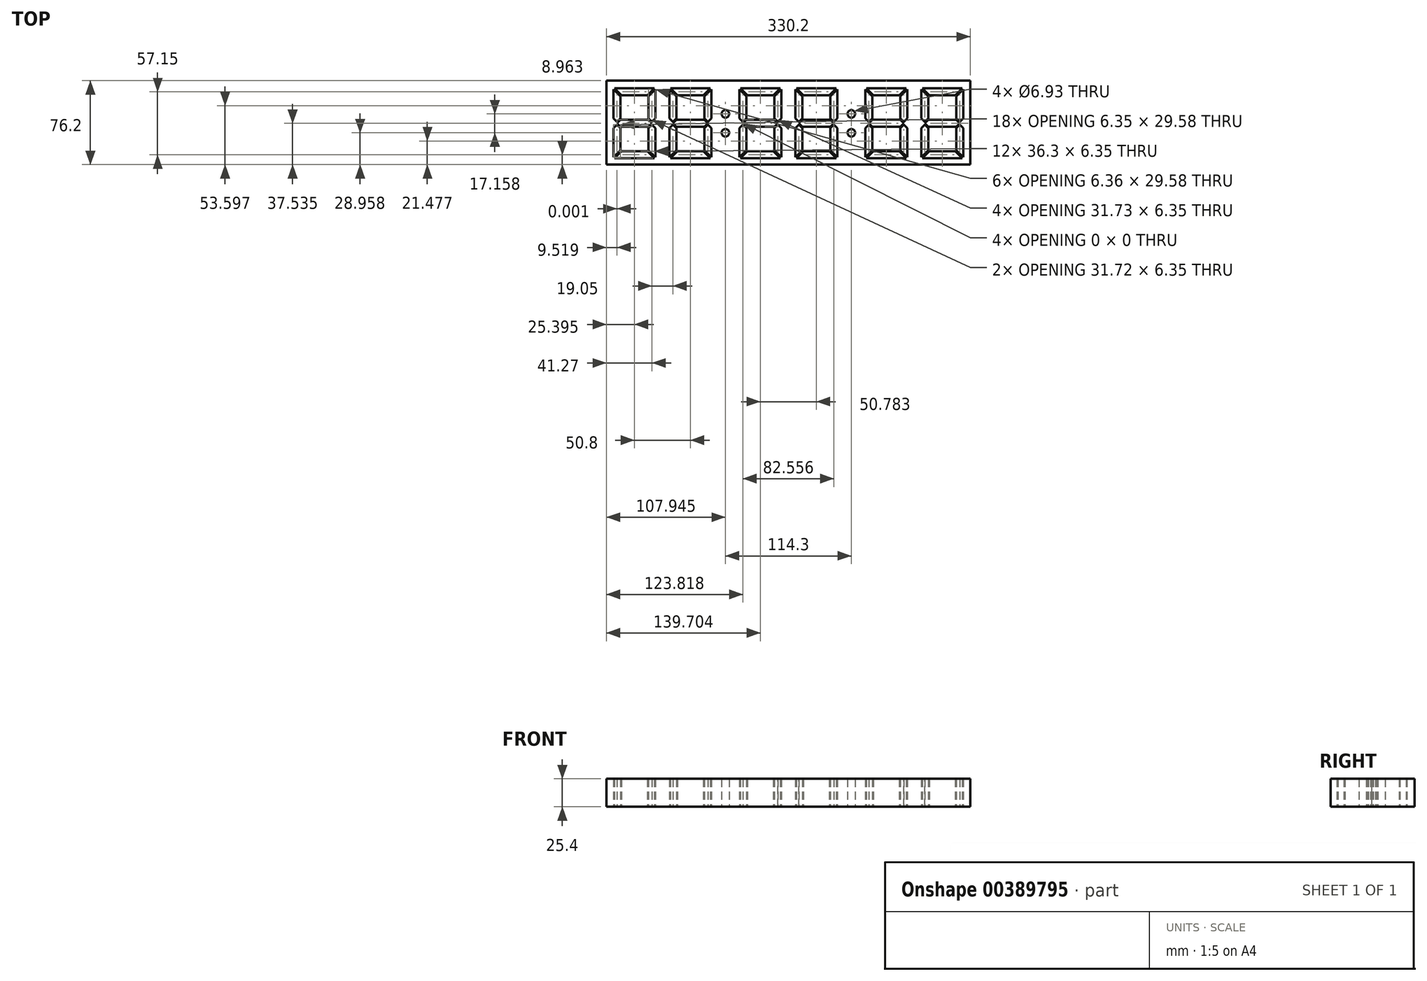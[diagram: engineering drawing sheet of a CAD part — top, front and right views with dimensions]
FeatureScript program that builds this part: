
annotation { "Feature Type Name" : "Feature", "Feature Type Description" : "" }
export const myFeature = defineFeature(function(context is Context, id is Id, definition is map)
    precondition{}
    {
        {
            var Q0;
            Q0=qCreatedBy(makeId("Top.planeOp"),FACE);
            var sketch = newSketch(context, id + "F0", { "sketchPlane" : qUnion([Q0])});
            skLineSegment(sketch, "E0.bottom", {"start": v(-71.32, 52.19) * mm, "end": v(-45.92, 52.19) * mm});
            skLineSegment(sketch, "E1.bottom", {"start": v(-64.08, 45.28) * mm, "end": v(-27.77, 45.28) * mm});
            skLineSegment(sketch, "E1.top", {"start": v(-64.08, -18.22) * mm, "end": v(-27.77, -18.22) * mm});
            skLineSegment(sketch, "E1.left", {"start": v(-64.98, 44.38) * mm, "end": v(-64.98, 18.04) * mm});
            skLineSegment(sketch, "E1.right", {"start": v(-26.87, 44.38) * mm, "end": v(-26.87, 18.04) * mm});
            skLineSegment(sketch, "E2.bottom", {"start": v(-57.73, 38.93) * mm, "end": v(-34.12, 38.93) * mm});
            skLineSegment(sketch, "E2.top", {"start": v(-57.73, -11.87) * mm, "end": v(-34.12, -11.87) * mm});
            skLineSegment(sketch, "E2.left", {"start": v(-58.62, 38.03) * mm, "end": v(-58.62, 17.97) * mm});
            skLineSegment(sketch, "E2.right", {"start": v(-33.22, 38.03) * mm, "end": v(-33.22, 17.97) * mm});
            skLineSegment(sketch, "E3", {"start": v(-45.92, 52.19) * mm, "end": v(-20.52, 52.19) * mm});
            skLineSegment(sketch, "E4", {"start": v(-61.35, 42.55) * mm, "end": v(-57.73, 38.93) * mm});
            skLineSegment(sketch, "E5", {"start": v(-62.25, 41.65) * mm, "end": v(-58.62, 38.03) * mm});
            skLineSegment(sketch, "E6", {"start": v(-62.25, 41.65) * mm, "end": v(-64.98, 44.38) * mm});
            skLineSegment(sketch, "E7", {"start": v(-61.35, 42.55) * mm, "end": v(-64.08, 45.28) * mm});
            skPoint(sketch, "E8.orphan", {"position": v(-64.98, 45.28) * mm});
            skPoint(sketch, "E9.orphan", {"position": v(-58.62, 38.93) * mm});
            skPoint(sketch, "E10.start.orphan", {"position": v(-61.8, 42.1) * mm});
            skLineSegment(sketch, "E11.MirrorCS", {"start": v(-29.6, 41.65) * mm, "end": v(-33.22, 38.03) * mm});
            skLineSegment(sketch, "E12.MirrorCS", {"start": v(-30.5, 42.55) * mm, "end": v(-34.12, 38.93) * mm});
            skPoint(sketch, "E13.MirrorP", {"position": v(-30.05, 42.1) * mm});
            skPoint(sketch, "E14.MirrorP", {"position": v(-26.87, 45.28) * mm});
            skLineSegment(sketch, "E15.MirrorCS", {"start": v(-30.5, 42.55) * mm, "end": v(-27.77, 45.28) * mm});
            skLineSegment(sketch, "E16.MirrorCS", {"start": v(-29.6, 41.65) * mm, "end": v(-26.87, 44.38) * mm});
            skPoint(sketch, "E17.MirrorP", {"position": v(-33.22, 38.93) * mm});
            skLineSegment(sketch, "E18.MirrorCS", {"start": v(-61.35, -15.5) * mm, "end": v(-57.73, -11.87) * mm});
            skPoint(sketch, "E19.MirrorP", {"position": v(-64.97, -18.22) * mm});
            skPoint(sketch, "E20.MirrorP", {"position": v(-61.8, -15.05) * mm});
            skLineSegment(sketch, "E21.MirrorCS", {"start": v(-29.6, -14.6) * mm, "end": v(-26.87, -17.32) * mm});
            skLineSegment(sketch, "E22.MirrorCS", {"start": v(-26.87, -17.32) * mm, "end": v(-26.87, 9) * mm});
            skLineSegment(sketch, "E23.MirrorCS", {"start": v(-29.6, -14.6) * mm, "end": v(-33.22, -10.97) * mm});
            skLineSegment(sketch, "E24.MirrorCS", {"start": v(-62.25, -14.6) * mm, "end": v(-64.98, -17.33) * mm});
            skPoint(sketch, "E25.MirrorP", {"position": v(-30.05, -15.05) * mm});
            skLineSegment(sketch, "E26.MirrorCS", {"start": v(-30.5, -15.5) * mm, "end": v(-27.77, -18.22) * mm});
            skPoint(sketch, "E27.MirrorP", {"position": v(-26.87, -18.22) * mm});
            skLineSegment(sketch, "E28.MirrorCS", {"start": v(-30.5, -15.5) * mm, "end": v(-34.12, -11.87) * mm});
            skPoint(sketch, "E29.MirrorP", {"position": v(-33.22, -11.87) * mm});
            skPoint(sketch, "E30.MirrorP", {"position": v(-58.62, -11.87) * mm});
            skLineSegment(sketch, "E31.MirrorCS", {"start": v(-64.98, -17.33) * mm, "end": v(-64.98, 9.01) * mm});
            skLineSegment(sketch, "E32.MirrorCS", {"start": v(-61.35, -15.5) * mm, "end": v(-64.08, -18.22) * mm});
            skPoint(sketch, "E33.MirrorCS.end.orphan", {"position": v(-42, 45.28) * mm});
            skPoint(sketch, "E33.MirrorCS.start.orphan", {"position": v(-42, 38.93) * mm});
            skPoint(sketch, "E34.end.orphan", {"position": v(-49.84, 45.28) * mm});
            skPoint(sketch, "E34.start.orphan", {"position": v(-49.84, 38.93) * mm});
            skPoint(sketch, "E35.end.orphan", {"position": v(-45.92, -24.57) * mm});
            skPoint(sketch, "E36.MirrorCS.end.orphan", {"position": v(-49.84, -18.22) * mm});
            skPoint(sketch, "E36.MirrorCS.start.orphan", {"position": v(-49.84, -11.87) * mm});
            skPoint(sketch, "E37.MirrorCS.end.orphan", {"position": v(-42, -18.22) * mm});
            skPoint(sketch, "E37.MirrorCS.start.orphan", {"position": v(-42, -11.87) * mm});
            skPoint(sketch, "E38.orphan", {"position": v(-58.62, 12.9) * mm});
            skPoint(sketch, "E39.orphan", {"position": v(-58.62, 14.16) * mm});
            skPoint(sketch, "E40.end.orphan", {"position": v(-64.97, 17.68) * mm});
            skPoint(sketch, "E41.MirrorCS.start.orphan", {"position": v(-58.3, 16.78) * mm});
            skPoint(sketch, "E42.MirrorCS.end.orphan", {"position": v(-64.97, 13.53) * mm});
            skPoint(sketch, "E43.MirrorP", {"position": v(-58.3, 10.28) * mm});
            skPoint(sketch, "E44.end.orphan", {"position": v(-64.98, 13.53) * mm});
            skLineSegment(sketch, "E45.trimOffspring", {"start": v(-64.98, 9.01) * mm, "end": v(-64.98, -17.33) * mm});
            skLineSegment(sketch, "E46.trimOffspring", {"start": v(-58.63, 9.08) * mm, "end": v(-58.63, -10.98) * mm});
            skPoint(sketch, "E47.trimOffspring.start.orphan", {"position": v(-64.97, 16.77) * mm});
            skPoint(sketch, "E48.trimOffspring.end.orphan", {"position": v(-26.87, 13.53) * mm});
            skLineSegment(sketch, "E49.MirrorCS", {"start": v(-26.87, 9) * mm, "end": v(-26.87, -17.32) * mm});
            skPoint(sketch, "E50.MirrorP", {"position": v(-33.54, 10.28) * mm});
            skPoint(sketch, "E51.MirrorP", {"position": v(-33.22, 12.9) * mm});
            skPoint(sketch, "E52.MirrorP", {"position": v(-33.54, 16.78) * mm});
            skLineSegment(sketch, "E53.MirrorCS", {"start": v(-26.87, -17.5) * mm, "end": v(-26.87, 9) * mm});
            skLineSegment(sketch, "E54.MirrorCS", {"start": v(-33.22, 9.08) * mm, "end": v(-33.22, -10.97) * mm});
            skPoint(sketch, "E55.MirrorP", {"position": v(-26.87, 16.77) * mm});
            skPoint(sketch, "E56.MirrorP", {"position": v(-26.87, 17.68) * mm});
            skPoint(sketch, "E57.MirrorP", {"position": v(-33.22, 14.16) * mm});
            skPoint(sketch, "E58.orphan", {"position": v(-64.98, -18.22) * mm});
            skLineSegment(sketch, "E59", {"start": v(-62.25, -14.6) * mm, "end": v(-58.63, -10.98) * mm});
            skLineSegment(sketch, "E60", {"start": v(-58.62, 16.7) * mm, "end": v(-61.78, 13.54) * mm});
            skPoint(sketch, "E61.trimOffspring.end.orphan", {"position": v(-58.62, 13.97) * mm});
            skPoint(sketch, "E62.right.start.orphan", {"position": v(-58.62, 13.53) * mm});
            skPoint(sketch, "E63.trimOffspring.end.orphan", {"position": v(-71.32, 13.8) * mm});
            skPoint(sketch, "E64.orphan", {"position": v(-61.8, 16.7) * mm});
            skLineSegment(sketch, "E65", {"start": v(-61.77, 14.8) * mm, "end": v(-58.62, 17.97) * mm});
            skLineSegment(sketch, "E66.MirrorCS", {"start": v(-61.77, 14.8) * mm, "end": v(-64.9, 17.97) * mm});
            skPoint(sketch, "E67.MirrorP", {"position": v(-61.8, 10.35) * mm});
            skLineSegment(sketch, "E68.MirrorCS", {"start": v(-61.77, 12.25) * mm, "end": v(-58.63, 9.08) * mm});
            skLineSegment(sketch, "E69.MirrorCS", {"start": v(-61.77, 12.25) * mm, "end": v(-64.9, 9.08) * mm});
            skLineSegment(sketch, "E70", {"start": v(-58.62, 16.7) * mm, "end": v(-33.22, 16.7) * mm});
            skLineSegment(sketch, "E71", {"start": v(-58.63, 10.35) * mm, "end": v(-33.23, 10.35) * mm});
            skLineSegment(sketch, "E72", {"start": v(-61.78, 13.54) * mm, "end": v(-58.63, 10.35) * mm});
            skLineSegment(sketch, "E73", {"start": v(-64.9, 17.97) * mm, "end": v(-64.98, 18.04) * mm});
            skPoint(sketch, "E74.orphan", {"position": v(-64.98, 17.1) * mm});
            skPoint(sketch, "E75.end.orphan", {"position": v(-64.97, 16.7) * mm});
            skPoint(sketch, "E76.trimOffspring.end.orphan", {"position": v(-58.63, 9.96) * mm});
            skLineSegment(sketch, "E77", {"start": v(-64.9, 9.08) * mm, "end": v(-64.98, 9.01) * mm});
            skPoint(sketch, "E78.orphan", {"position": v(-64.98, 9.96) * mm});
            skLineSegment(sketch, "E79.MirrorCS", {"start": v(-30.08, 14.8) * mm, "end": v(-33.22, 17.97) * mm});
            skLineSegment(sketch, "E80.MirrorCS", {"start": v(-30.08, 14.8) * mm, "end": v(-26.94, 17.97) * mm});
            skLineSegment(sketch, "E81.MirrorCS", {"start": v(-33.22, 16.7) * mm, "end": v(-30.07, 13.54) * mm});
            skLineSegment(sketch, "E82.MirrorCS", {"start": v(-30.07, 13.54) * mm, "end": v(-33.22, 10.35) * mm});
            skLineSegment(sketch, "E83.MirrorCS", {"start": v(-30.08, 12.26) * mm, "end": v(-33.22, 9.08) * mm});
            skLineSegment(sketch, "E84.MirrorCS", {"start": v(-30.08, 12.26) * mm, "end": v(-26.94, 9.08) * mm});
            skPoint(sketch, "E85.orphan", {"position": v(-33.22, 13.53) * mm});
            skPoint(sketch, "E86.orphan", {"position": v(-33.22, 9.96) * mm});
            skLineSegment(sketch, "E87", {"start": v(-26.94, 9.08) * mm, "end": v(-26.87, 9) * mm});
            skPoint(sketch, "E88.orphan", {"position": v(-33.22, 17.1) * mm});
            skLineSegment(sketch, "E89", {"start": v(-26.94, 17.97) * mm, "end": v(-26.87, 18.04) * mm});
            skPoint(sketch, "E90.end.orphan", {"position": v(-26.87, 16.7) * mm});
            skLineSegment(sketch, "E91.bottom", {"start": v(-20.52, 52.19) * mm, "end": v(-14.17, 52.19) * mm});
            skLineSegment(sketch, "E91.top", {"start": v(-20.52, -24.01) * mm, "end": v(-7.82, -24.01) * mm});
            skLineSegment(sketch, "E92", {"start": v(-14.17, 52.19) * mm, "end": v(-7.82, 52.19) * mm});
            skCircle(sketch, "E93", {"center": v(-14.17, 22.1) * mm, "radius": 3.46 * mm});
            skPoint(sketch, "E94.orphan", {"position": v(-14.17, 52.19) * mm});
            skPoint(sketch, "E95.trimOffspring.end.orphan", {"position": v(-14.17, -24.01) * mm});
            skCircle(sketch, "E96.MirrorC", {"center": v(-14.17, 4.95) * mm, "radius": 3.46 * mm});
            skPoint(sketch, "E97.end.orphan", {"position": v(-7.82, 14.09) * mm});
            skPoint(sketch, "E98.end.orphan", {"position": v(-20.52, -24.57) * mm});
            skPoint(sketch, "E98.start.orphan", {"position": v(-20.52, 13.53) * mm});
            skPoint(sketch, "E99.start.orphan", {"position": v(-20.52, 13.8) * mm});
            skPoint(sketch, "E100.MirrorP", {"position": v(-77.67, 13.53) * mm});
            skPoint(sketch, "E101.MirrorP", {"position": v(-115.77, 13.53) * mm});
            skLineSegment(sketch, "E102.MirrorCS", {"start": v(-77.74, 9.08) * mm, "end": v(-77.67, 9.01) * mm});
            skLineSegment(sketch, "E103.MirrorCS", {"start": v(-115.7, 9.08) * mm, "end": v(-115.78, 9) * mm});
            skLineSegment(sketch, "E104.MirrorCS", {"start": v(-115.7, 17.97) * mm, "end": v(-115.77, 18.04) * mm});
            skLineSegment(sketch, "E105.MirrorCS", {"start": v(-109.42, 16.7) * mm, "end": v(-112.58, 13.54) * mm});
            skLineSegment(sketch, "E106.MirrorCS", {"start": v(-80.87, 13.54) * mm, "end": v(-84.02, 10.35) * mm});
            skLineSegment(sketch, "E107.MirrorCS", {"start": v(-84.03, 16.7) * mm, "end": v(-80.87, 13.54) * mm});
            skLineSegment(sketch, "E108.MirrorCS", {"start": v(-112.58, 13.54) * mm, "end": v(-109.42, 10.35) * mm});
            skLineSegment(sketch, "E109.MirrorCS", {"start": v(-77.74, 17.97) * mm, "end": v(-77.67, 18.04) * mm});
            skLineSegment(sketch, "E110.MirrorCS", {"start": v(-115.78, 9) * mm, "end": v(-115.77, -17.32) * mm});
            skLineSegment(sketch, "E111.MirrorCS", {"start": v(-80.88, 14.8) * mm, "end": v(-84.03, 17.97) * mm});
            skLineSegment(sketch, "E112.MirrorCS", {"start": v(-113.05, -14.6) * mm, "end": v(-115.77, -17.32) * mm});
            skLineSegment(sketch, "E113.MirrorCS", {"start": v(-80.88, 14.8) * mm, "end": v(-77.74, 17.97) * mm});
            skLineSegment(sketch, "E114.MirrorCS", {"start": v(-80.4, -14.6) * mm, "end": v(-77.67, -17.33) * mm});
            skLineSegment(sketch, "E115.MirrorCS", {"start": v(-80.88, 12.25) * mm, "end": v(-84.02, 9.08) * mm});
            skLineSegment(sketch, "E116.MirrorCS", {"start": v(-112.15, -15.5) * mm, "end": v(-114.88, -18.22) * mm});
            skLineSegment(sketch, "E117.MirrorCS", {"start": v(-80.88, 12.25) * mm, "end": v(-77.74, 9.08) * mm});
            skLineSegment(sketch, "E118.MirrorCS", {"start": v(-113.05, 41.65) * mm, "end": v(-115.77, 44.38) * mm});
            skLineSegment(sketch, "E119.MirrorCS", {"start": v(-81.3, -15.5) * mm, "end": v(-78.57, -18.22) * mm});
            skLineSegment(sketch, "E120.MirrorCS", {"start": v(-81.3, 42.55) * mm, "end": v(-78.57, 45.28) * mm});
            skLineSegment(sketch, "E121.MirrorCS", {"start": v(-112.57, 14.8) * mm, "end": v(-115.7, 17.97) * mm});
            skLineSegment(sketch, "E122.MirrorCS", {"start": v(-112.57, 14.8) * mm, "end": v(-109.42, 17.97) * mm});
            skLineSegment(sketch, "E123.MirrorCS", {"start": v(-112.15, 42.55) * mm, "end": v(-114.88, 45.28) * mm});
            skPoint(sketch, "E124.MirrorP", {"position": v(-84.02, 13.53) * mm});
            skLineSegment(sketch, "E125.MirrorCS", {"start": v(-109.42, 9.08) * mm, "end": v(-109.42, -10.97) * mm});
            skPoint(sketch, "E126.MirrorP", {"position": v(-84.02, 12.9) * mm});
            skLineSegment(sketch, "E127.MirrorCS", {"start": v(-109.42, 38.03) * mm, "end": v(-109.42, 17.97) * mm});
            skLineSegment(sketch, "E128.MirrorCS", {"start": v(-112.57, 12.26) * mm, "end": v(-109.42, 9.08) * mm});
            skLineSegment(sketch, "E129.MirrorCS", {"start": v(-115.77, 44.38) * mm, "end": v(-115.77, 18.04) * mm});
            skLineSegment(sketch, "E130.MirrorCS", {"start": v(-112.57, 12.26) * mm, "end": v(-115.7, 9.08) * mm});
            skLineSegment(sketch, "E131.MirrorCS", {"start": v(-80.4, 41.65) * mm, "end": v(-77.67, 44.38) * mm});
            skLineSegment(sketch, "E132.MirrorCS", {"start": v(-112.15, 42.55) * mm, "end": v(-108.53, 38.93) * mm});
            skPoint(sketch, "E133.MirrorP", {"position": v(-109.1, 16.78) * mm});
            skPoint(sketch, "E134.MirrorP", {"position": v(-109.1, 10.28) * mm});
            skPoint(sketch, "E135.MirrorP", {"position": v(-109.42, 12.9) * mm});
            skLineSegment(sketch, "E136.MirrorCS", {"start": v(-113.05, -14.6) * mm, "end": v(-109.42, -10.97) * mm});
            skPoint(sketch, "E137.MirrorP", {"position": v(-115.77, -18.22) * mm});
            skLineSegment(sketch, "E138.MirrorCS", {"start": v(-81.3, -15.5) * mm, "end": v(-84.92, -11.87) * mm});
            skLineSegment(sketch, "E139.MirrorCS", {"start": v(-81.3, 42.55) * mm, "end": v(-84.92, 38.93) * mm});
            skLineSegment(sketch, "E140.MirrorCS", {"start": v(-80.4, -14.6) * mm, "end": v(-84.02, -10.98) * mm});
            skPoint(sketch, "E141.MirrorP", {"position": v(-115.77, 45.28) * mm});
            skLineSegment(sketch, "E142.MirrorCS", {"start": v(-84.92, -11.87) * mm, "end": v(-108.53, -11.87) * mm});
            skPoint(sketch, "E143.MirrorP", {"position": v(-109.42, 13.53) * mm});
            skLineSegment(sketch, "E144.MirrorCS", {"start": v(-77.67, -17.33) * mm, "end": v(-77.67, 9.01) * mm});
            skPoint(sketch, "E145.MirrorP", {"position": v(-77.67, 16.77) * mm});
            skLineSegment(sketch, "E146.MirrorCS", {"start": v(-113.05, 41.65) * mm, "end": v(-109.42, 38.03) * mm});
            skPoint(sketch, "E147.MirrorP", {"position": v(-109.42, 14.16) * mm});
            skPoint(sketch, "E148.MirrorP", {"position": v(-122.12, 13.53) * mm});
            skPoint(sketch, "E149.MirrorP", {"position": v(-77.67, -18.22) * mm});
            skLineSegment(sketch, "E150.MirrorCS", {"start": v(-78.57, -18.22) * mm, "end": v(-114.88, -18.22) * mm});
            skPoint(sketch, "E151.MirrorP", {"position": v(-84.34, 16.78) * mm});
            skLineSegment(sketch, "E152.MirrorCS", {"start": v(-112.15, -15.5) * mm, "end": v(-108.53, -11.87) * mm});
            skPoint(sketch, "E153.MirrorP", {"position": v(-84.34, 10.28) * mm});
            skPoint(sketch, "E154.MirrorP", {"position": v(-84.03, 14.16) * mm});
            skLineSegment(sketch, "E155.MirrorCS", {"start": v(-115.77, -17.5) * mm, "end": v(-115.78, 9) * mm});
            skPoint(sketch, "E156.MirrorP", {"position": v(-115.78, 16.7) * mm});
            skLineSegment(sketch, "E157.MirrorCS", {"start": v(-80.4, 41.65) * mm, "end": v(-84.03, 38.03) * mm});
            skPoint(sketch, "E158.MirrorP", {"position": v(-84.02, 13.97) * mm});
            skLineSegment(sketch, "E159.MirrorCS", {"start": v(-115.77, -17.32) * mm, "end": v(-115.78, 9) * mm});
            skPoint(sketch, "E160.MirrorP", {"position": v(-109.42, -11.87) * mm});
            skPoint(sketch, "E161.MirrorP", {"position": v(-77.67, 45.28) * mm});
            skPoint(sketch, "E162.MirrorP", {"position": v(-77.68, 16.7) * mm});
            skPoint(sketch, "E163.MirrorP", {"position": v(-77.67, 9.96) * mm});
            skPoint(sketch, "E164.MirrorP", {"position": v(-92.8, -11.87) * mm});
            skPoint(sketch, "E165.MirrorP", {"position": v(-80.85, 42.1) * mm});
            skLineSegment(sketch, "E166.MirrorCS", {"start": v(-84.02, 9.08) * mm, "end": v(-84.02, -10.98) * mm});
            skPoint(sketch, "E167.MirrorP", {"position": v(-92.8, -18.22) * mm});
            skLineSegment(sketch, "E168.MirrorCS", {"start": v(-77.67, 9.01) * mm, "end": v(-77.67, -17.33) * mm});
            skPoint(sketch, "E169.MirrorP", {"position": v(-84.02, -11.87) * mm});
            skPoint(sketch, "E170.MirrorP", {"position": v(-100.64, 45.28) * mm});
            skPoint(sketch, "E171.MirrorP", {"position": v(-84.03, 38.93) * mm});
            skPoint(sketch, "E172.MirrorP", {"position": v(-84.02, 9.96) * mm});
            skPoint(sketch, "E173.MirrorP", {"position": v(-109.42, 9.96) * mm});
            skPoint(sketch, "E174.MirrorP", {"position": v(-109.42, 17.1) * mm});
            skPoint(sketch, "E175.MirrorP", {"position": v(-115.78, 16.77) * mm});
            skLineSegment(sketch, "E176.MirrorCS", {"start": v(-84.92, 38.93) * mm, "end": v(-108.53, 38.93) * mm});
            skPoint(sketch, "E177.MirrorP", {"position": v(-100.64, -18.22) * mm});
            skPoint(sketch, "E178.MirrorP", {"position": v(-115.77, 17.68) * mm});
            skPoint(sketch, "E179.MirrorP", {"position": v(-100.64, 38.93) * mm});
            skPoint(sketch, "E180.MirrorP", {"position": v(-80.85, 10.35) * mm});
            skPoint(sketch, "E181.MirrorP", {"position": v(-100.64, -11.87) * mm});
            skPoint(sketch, "E182.MirrorP", {"position": v(-92.8, 38.93) * mm});
            skPoint(sketch, "E183.MirrorP", {"position": v(-109.42, 38.93) * mm});
            skLineSegment(sketch, "E184.MirrorCS", {"start": v(-77.67, 44.38) * mm, "end": v(-77.67, 18.04) * mm});
            skPoint(sketch, "E185.MirrorP", {"position": v(-77.67, 17.1) * mm});
            skPoint(sketch, "E186.MirrorP", {"position": v(-112.6, 42.1) * mm});
            skLineSegment(sketch, "E187.MirrorCS", {"start": v(-84.03, 16.7) * mm, "end": v(-109.43, 16.7) * mm});
            skLineSegment(sketch, "E188.MirrorCS", {"start": v(-84.02, 10.35) * mm, "end": v(-109.42, 10.35) * mm});
            skLineSegment(sketch, "E189.MirrorCS", {"start": v(-84.03, 38.03) * mm, "end": v(-84.03, 17.97) * mm});
            skPoint(sketch, "E190.MirrorP", {"position": v(-112.6, -15.05) * mm});
            skPoint(sketch, "E191.MirrorP", {"position": v(-80.85, 16.7) * mm});
            skPoint(sketch, "E192.MirrorP", {"position": v(-77.67, 17.68) * mm});
            skPoint(sketch, "E193.MirrorP", {"position": v(-92.8, 45.28) * mm});
            skPoint(sketch, "E194.MirrorP", {"position": v(-80.85, -15.05) * mm});
            skPoint(sketch, "E195.MirrorP", {"position": v(-122.13, 13.8) * mm});
            skLineSegment(sketch, "E196.MirrorCS", {"start": v(-78.57, 45.28) * mm, "end": v(-114.88, 45.28) * mm});
            skLineSegment(sketch, "E197.bottom", {"start": v(-71.32, 52.19) * mm, "end": v(-122.12, 52.19) * mm});
            skLineSegment(sketch, "E197.top", {"start": v(-71.32, -24.01) * mm, "end": v(-122.12, -24.01) * mm});
            skLineSegment(sketch, "E197.right", {"start": v(-122.12, 52.19) * mm, "end": v(-122.12, -24.01) * mm});
            skLineSegment(sketch, "E198", {"start": v(-20.52, -24.01) * mm, "end": v(-71.32, -24.01) * mm});
            skPoint(sketch, "E199.orphan", {"position": v(-71.32, -24.57) * mm});
            skPoint(sketch, "E200.MirrorCS.start.orphan", {"position": v(-20.52, 51.63) * mm});
            skPoint(sketch, "E201.1.0.0", {"position": v(-7.83, 13.8) * mm});
            skLineSegment(sketch, "E201.1.0.1", {"start": v(93.78, 52.19) * mm, "end": v(100.13, 52.19) * mm});
            skLineSegment(sketch, "E201.1.0.2", {"start": v(30.28, 9.08) * mm, "end": v(30.28, -10.98) * mm});
            skLineSegment(sketch, "E201.1.0.3", {"start": v(30.27, 16.7) * mm, "end": v(4.87, 16.7) * mm});
            skPoint(sketch, "E201.1.0.4", {"position": v(81.08, -11.87) * mm});
            skLineSegment(sketch, "E201.1.0.5", {"start": v(93.78, -24.01) * mm, "end": v(106.48, -24.01) * mm});
            skPoint(sketch, "E201.1.0.6", {"position": v(72.3, -11.87) * mm});
            skPoint(sketch, "E201.1.0.7", {"position": v(52.5, -15.05) * mm});
            skPoint(sketch, "E201.1.0.8", {"position": v(33.45, 10.35) * mm});
            skLineSegment(sketch, "E201.1.0.9", {"start": v(35.73, 45.28) * mm, "end": v(-0.58, 45.28) * mm});
            skLineSegment(sketch, "E201.1.0.10", {"start": v(-1.47, 44.38) * mm, "end": v(-1.47, 18.04) * mm});
            skPoint(sketch, "E201.1.0.11", {"position": v(21.5, -18.22) * mm});
            skPoint(sketch, "E201.1.0.12", {"position": v(36.63, 9.96) * mm});
            skPoint(sketch, "E201.1.0.13", {"position": v(49.32, 9.96) * mm});
            skPoint(sketch, "E201.1.0.14", {"position": v(84.25, -15.05) * mm});
            skLineSegment(sketch, "E201.1.0.15", {"start": v(55.67, 10.35) * mm, "end": v(81.07, 10.35) * mm});
            skPoint(sketch, "E201.1.0.16", {"position": v(81.08, 38.93) * mm});
            skPoint(sketch, "E201.1.0.17", {"position": v(87.43, 45.28) * mm});
            skCircle(sketch, "E201.1.0.18", {"center": v(100.13, 4.95) * mm, "radius": 3.46 * mm});
            skPoint(sketch, "E201.1.0.19", {"position": v(42.98, -24.57) * mm});
            skLineSegment(sketch, "E201.1.0.20", {"start": v(81.08, 9.08) * mm, "end": v(81.08, -10.97) * mm});
            skPoint(sketch, "E201.1.0.21", {"position": v(33.45, -15.05) * mm});
            skPoint(sketch, "E201.1.0.22", {"position": v(29.96, 16.78) * mm});
            skPoint(sketch, "E201.1.0.23", {"position": v(81.08, 17.1) * mm});
            skPoint(sketch, "E201.1.0.25", {"position": v(49.33, 17.68) * mm});
            skPoint(sketch, "E201.1.0.26", {"position": v(72.3, 38.93) * mm});
            skLineSegment(sketch, "E201.1.0.27", {"start": v(29.38, 38.93) * mm, "end": v(5.77, 38.93) * mm});
            skPoint(sketch, "E201.1.0.28", {"position": v(81.08, 9.96) * mm});
            skLineSegment(sketch, "E201.1.0.29", {"start": v(4.88, 9.08) * mm, "end": v(4.88, -10.97) * mm});
            skPoint(sketch, "E201.1.0.30", {"position": v(55.68, 13.97) * mm});
            skPoint(sketch, "E201.1.0.31", {"position": v(-1.47, 17.68) * mm});
            skPoint(sketch, "E201.1.0.32", {"position": v(13.66, 38.93) * mm});
            skLineSegment(sketch, "E201.1.0.34", {"start": v(56.57, 38.93) * mm, "end": v(80.18, 38.93) * mm});
            skLineSegment(sketch, "E201.1.0.35", {"start": v(49.32, 44.38) * mm, "end": v(49.32, 18.04) * mm});
            skLineSegment(sketch, "E201.1.0.36", {"start": v(42.98, 52.19) * mm, "end": v(68.38, 52.19) * mm});
            skLineSegment(sketch, "E201.1.0.37", {"start": v(42.98, -24.01) * mm, "end": v(-7.82, -24.01) * mm});
            skPoint(sketch, "E201.1.0.38", {"position": v(36.63, -18.22) * mm});
            skPoint(sketch, "E201.1.0.39", {"position": v(30.28, 12.9) * mm});
            skPoint(sketch, "E201.1.0.40", {"position": v(87.43, 16.77) * mm});
            skPoint(sketch, "E201.1.0.41", {"position": v(30.27, 14.16) * mm});
            skPoint(sketch, "E201.1.0.42", {"position": v(13.66, 45.28) * mm});
            skPoint(sketch, "E201.1.0.43", {"position": v(-1.47, 13.53) * mm});
            skPoint(sketch, "E201.1.0.44", {"position": v(64.46, -11.87) * mm});
            skPoint(sketch, "E201.1.0.45", {"position": v(52.5, 42.1) * mm});
            skLineSegment(sketch, "E201.1.0.46", {"start": v(55.67, 9.08) * mm, "end": v(55.67, -10.98) * mm});
            skPoint(sketch, "E201.1.0.47", {"position": v(33.45, 16.7) * mm});
            skPoint(sketch, "E201.1.0.48", {"position": v(-1.47, 45.28) * mm});
            skLineSegment(sketch, "E201.1.0.49", {"start": v(93.78, -24.01) * mm, "end": v(42.98, -24.01) * mm});
            skPoint(sketch, "E201.1.0.50", {"position": v(49.32, 45.28) * mm});
            skPoint(sketch, "E201.1.0.51", {"position": v(56, 10.28) * mm});
            skLineSegment(sketch, "E201.1.0.52", {"start": v(55.68, 38.03) * mm, "end": v(55.68, 17.97) * mm});
            skLineSegment(sketch, "E201.1.0.53", {"start": v(42.98, 52.19) * mm, "end": v(-7.82, 52.19) * mm});
            skPoint(sketch, "E201.1.0.54", {"position": v(93.78, 13.8) * mm});
            skPoint(sketch, "E201.1.0.55", {"position": v(87.43, 13.53) * mm});
            skPoint(sketch, "E201.1.0.56", {"position": v(64.46, 45.28) * mm});
            skPoint(sketch, "E201.1.0.57", {"position": v(5.2, 16.78) * mm});
            skPoint(sketch, "E201.1.0.58", {"position": v(80.76, 10.28) * mm});
            skPoint(sketch, "E201.1.0.59", {"position": v(55.67, 9.96) * mm});
            skPoint(sketch, "E201.1.0.60", {"position": v(72.3, 45.28) * mm});
            skPoint(sketch, "E201.1.0.61", {"position": v(49.32, -18.22) * mm});
            skPoint(sketch, "E201.1.0.62", {"position": v(42.98, 13.8) * mm});
            skPoint(sketch, "E201.1.0.63", {"position": v(55.68, 13.53) * mm});
            skPoint(sketch, "E201.1.0.64", {"position": v(55.68, -11.87) * mm});
            skPoint(sketch, "E201.1.0.65", {"position": v(106.48, 14.09) * mm});
            skPoint(sketch, "E201.1.0.66", {"position": v(93.78, 13.53) * mm});
            skLineSegment(sketch, "E201.1.0.67", {"start": v(100.13, 52.19) * mm, "end": v(106.48, 52.19) * mm});
            skPoint(sketch, "E201.1.0.68", {"position": v(4.88, 12.9) * mm});
            skPoint(sketch, "E201.1.0.69", {"position": v(49.32, 13.53) * mm});
            skPoint(sketch, "E201.1.0.70", {"position": v(100.13, 52.19) * mm});
            skPoint(sketch, "E201.1.0.71", {"position": v(30.28, -11.87) * mm});
            skPoint(sketch, "E201.1.0.72", {"position": v(1.7, -15.05) * mm});
            skLineSegment(sketch, "E201.1.0.73", {"start": v(87.43, 44.38) * mm, "end": v(87.43, 18.04) * mm});
            skPoint(sketch, "E201.1.0.74", {"position": v(68.38, -24.57) * mm});
            skPoint(sketch, "E201.1.0.75", {"position": v(55.68, 12.9) * mm});
            skPoint(sketch, "E201.1.0.76", {"position": v(49.32, 17.1) * mm});
            skPoint(sketch, "E201.1.0.77", {"position": v(4.88, -11.87) * mm});
            skLineSegment(sketch, "E201.1.0.78", {"start": v(49.32, 9.01) * mm, "end": v(49.32, -17.33) * mm});
            skPoint(sketch, "E201.1.0.79", {"position": v(64.46, 38.93) * mm});
            skLineSegment(sketch, "E201.1.0.80", {"start": v(56.57, -11.87) * mm, "end": v(80.18, -11.87) * mm});
            skLineSegment(sketch, "E201.1.0.81", {"start": v(4.88, 38.03) * mm, "end": v(4.88, 17.97) * mm});
            skPoint(sketch, "E201.1.0.82", {"position": v(1.7, 42.1) * mm});
            skPoint(sketch, "E201.1.0.83", {"position": v(52.5, 10.35) * mm});
            skPoint(sketch, "E201.1.0.84", {"position": v(49.33, 16.7) * mm});
            skPoint(sketch, "E201.1.0.85", {"position": v(36.63, 17.68) * mm});
            skPoint(sketch, "E201.1.0.86", {"position": v(64.46, -18.22) * mm});
            skPoint(sketch, "E201.1.0.87", {"position": v(81.08, 12.9) * mm});
            skPoint(sketch, "E201.1.0.88", {"position": v(55.68, 38.93) * mm});
            skPoint(sketch, "E201.1.0.89", {"position": v(5.2, 10.28) * mm});
            skPoint(sketch, "E201.1.0.90", {"position": v(36.63, 13.53) * mm});
            skPoint(sketch, "E201.1.0.91", {"position": v(93.78, -24.57) * mm});
            skLineSegment(sketch, "E201.1.0.92", {"start": v(50.22, 45.28) * mm, "end": v(86.53, 45.28) * mm});
            skLineSegment(sketch, "E201.1.0.93", {"start": v(50.22, -18.22) * mm, "end": v(86.53, -18.22) * mm});
            skPoint(sketch, "E201.1.0.94", {"position": v(30.28, 9.96) * mm});
            skPoint(sketch, "E201.1.0.95", {"position": v(29.96, 10.28) * mm});
            skLineSegment(sketch, "E201.1.0.96", {"start": v(30.27, 38.03) * mm, "end": v(30.27, 17.97) * mm});
            skLineSegment(sketch, "E201.1.0.97", {"start": v(30.28, 10.35) * mm, "end": v(4.88, 10.35) * mm});
            skPoint(sketch, "E201.1.0.98", {"position": v(87.43, -18.22) * mm});
            skPoint(sketch, "E201.1.0.99", {"position": v(52.5, 16.7) * mm});
            skPoint(sketch, "E201.1.0.100", {"position": v(30.27, 38.93) * mm});
            skLineSegment(sketch, "E201.1.0.101", {"start": v(-1.47, -17.32) * mm, "end": v(-1.48, 9) * mm});
            skPoint(sketch, "E201.1.0.102", {"position": v(36.63, 45.28) * mm});
            skPoint(sketch, "E201.1.0.103", {"position": v(4.88, 17.1) * mm});
            skPoint(sketch, "E201.1.0.104", {"position": v(4.88, 9.96) * mm});
            skLineSegment(sketch, "E201.1.0.105", {"start": v(68.38, 52.19) * mm, "end": v(93.78, 52.19) * mm});
            skLineSegment(sketch, "E201.1.0.106", {"start": v(29.38, -11.87) * mm, "end": v(5.77, -11.87) * mm});
            skPoint(sketch, "E201.1.0.107", {"position": v(13.66, -11.87) * mm});
            skPoint(sketch, "E201.1.0.108", {"position": v(93.78, 51.63) * mm});
            skPoint(sketch, "E201.1.0.109", {"position": v(-7.82, 13.53) * mm});
            skLineSegment(sketch, "E201.1.0.110", {"start": v(35.73, -18.22) * mm, "end": v(-0.58, -18.22) * mm});
            skPoint(sketch, "E201.1.0.111", {"position": v(4.88, 38.93) * mm});
            skPoint(sketch, "E201.1.0.112", {"position": v(21.5, -11.87) * mm});
            skLineSegment(sketch, "E201.1.0.113", {"start": v(36.63, 44.38) * mm, "end": v(36.63, 18.04) * mm});
            skCircle(sketch, "E201.1.0.114", {"center": v(100.13, 22.1) * mm, "radius": 3.46 * mm});
            skPoint(sketch, "E201.1.0.115", {"position": v(21.5, 45.28) * mm});
            skLineSegment(sketch, "E201.1.0.116", {"start": v(36.63, -17.33) * mm, "end": v(36.63, 9.01) * mm});
            skPoint(sketch, "E201.1.0.117", {"position": v(21.5, 38.93) * mm});
            skLineSegment(sketch, "E201.1.0.118", {"start": v(55.68, 16.7) * mm, "end": v(81.08, 16.7) * mm});
            skPoint(sketch, "E201.1.0.119", {"position": v(13.66, -18.22) * mm});
            skPoint(sketch, "E201.1.0.120", {"position": v(33.45, 42.1) * mm});
            skPoint(sketch, "E201.1.0.121", {"position": v(84.25, 42.1) * mm});
            skPoint(sketch, "E201.1.0.122", {"position": v(72.3, -18.22) * mm});
            skPoint(sketch, "E201.1.0.123", {"position": v(56, 16.78) * mm});
            skPoint(sketch, "E201.1.0.124", {"position": v(100.13, -24.01) * mm});
            skPoint(sketch, "E201.1.0.125", {"position": v(80.76, 16.78) * mm});
            skPoint(sketch, "E201.1.0.126", {"position": v(-1.47, -18.22) * mm});
            skLineSegment(sketch, "E201.1.0.127", {"start": v(81.08, 38.03) * mm, "end": v(81.08, 17.97) * mm});
            skPoint(sketch, "E201.1.0.128", {"position": v(-1.48, 16.77) * mm});
            skLineSegment(sketch, "E201.1.0.129", {"start": v(87.43, -17.5) * mm, "end": v(87.43, 9) * mm});
            skPoint(sketch, "E201.1.0.130", {"position": v(36.62, 16.7) * mm});
            skLineSegment(sketch, "E201.1.0.131", {"start": v(56.57, -11.87) * mm, "end": v(80.18, -11.87) * mm});
            skLineSegment(sketch, "E201.1.0.132", {"start": v(4.88, 9.08) * mm, "end": v(4.88, -10.97) * mm});
            skPoint(sketch, "E201.1.0.133", {"position": v(55.68, 14.16) * mm});
            skPoint(sketch, "E201.1.0.134", {"position": v(49.33, -18.22) * mm});
            skPoint(sketch, "E201.1.0.135", {"position": v(4.88, 12.9) * mm});
            skPoint(sketch, "E201.1.0.136", {"position": v(36.63, 17.1) * mm});
            skLineSegment(sketch, "E201.1.0.137", {"start": v(81.08, 9.08) * mm, "end": v(81.08, -10.97) * mm});
            skLineSegment(sketch, "E201.1.0.138", {"start": v(36.63, 9.01) * mm, "end": v(36.63, -17.33) * mm});
            skLineSegment(sketch, "E201.1.0.139", {"start": v(33, 42.55) * mm, "end": v(29.38, 38.93) * mm});
            skPoint(sketch, "E201.1.0.140", {"position": v(-1.47, 45.28) * mm});
            skLineSegment(sketch, "E201.1.0.141", {"start": v(52.05, -14.6) * mm, "end": v(55.67, -10.98) * mm});
            skLineSegment(sketch, "E201.1.0.142", {"start": v(1.25, 41.65) * mm, "end": v(4.88, 38.03) * mm});
            skLineSegment(sketch, "E201.1.0.143", {"start": v(84.7, -14.6) * mm, "end": v(81.08, -10.97) * mm});
            skLineSegment(sketch, "E201.1.0.144", {"start": v(52.95, -15.5) * mm, "end": v(56.57, -11.87) * mm});
            skPoint(sketch, "E201.1.0.145", {"position": v(5.2, 10.28) * mm});
            skPoint(sketch, "E201.1.0.146", {"position": v(81.08, 14.16) * mm});
            skPoint(sketch, "E201.1.0.147", {"position": v(56, 10.28) * mm});
            skPoint(sketch, "E201.1.0.148", {"position": v(49.33, 16.77) * mm});
            skPoint(sketch, "E201.1.0.149", {"position": v(87.43, 45.28) * mm});
            skPoint(sketch, "E201.1.0.150", {"position": v(87.43, 13.53) * mm});
            skPoint(sketch, "E201.1.0.151", {"position": v(55.68, 12.9) * mm});
            skPoint(sketch, "E201.1.0.152", {"position": v(93.78, -24.57) * mm});
            skPoint(sketch, "E201.1.0.153", {"position": v(4.88, 14.16) * mm});
            skLineSegment(sketch, "E201.1.0.154", {"start": v(33.9, -14.6) * mm, "end": v(30.28, -10.98) * mm});
            skLineSegment(sketch, "E201.1.0.155", {"start": v(29.38, -11.87) * mm, "end": v(5.77, -11.87) * mm});
            skPoint(sketch, "E201.1.0.156", {"position": v(87.43, -18.22) * mm});
            skPoint(sketch, "E201.1.0.157", {"position": v(5.2, 16.78) * mm});
            skPoint(sketch, "E201.1.0.158", {"position": v(87.43, 16.7) * mm});
            skLineSegment(sketch, "E201.1.0.159", {"start": v(33, -15.5) * mm, "end": v(29.38, -11.87) * mm});
            skLineSegment(sketch, "E201.1.0.160", {"start": v(83.8, -15.5) * mm, "end": v(80.18, -11.87) * mm});
            skLineSegment(sketch, "E201.1.0.161", {"start": v(-1.48, 9) * mm, "end": v(-1.47, -17.32) * mm});
            skLineSegment(sketch, "E201.1.0.162", {"start": v(52.95, 42.55) * mm, "end": v(56.57, 38.93) * mm});
            skLineSegment(sketch, "E201.1.0.163", {"start": v(87.43, 44.38) * mm, "end": v(87.43, 18.04) * mm});
            skLineSegment(sketch, "E201.1.0.164", {"start": v(33.9, 41.65) * mm, "end": v(30.27, 38.03) * mm});
            skPoint(sketch, "E201.1.0.165", {"position": v(49.33, 13.53) * mm});
            skLineSegment(sketch, "E201.1.0.166", {"start": v(83.8, 42.55) * mm, "end": v(80.18, 38.93) * mm});
            skLineSegment(sketch, "E201.1.0.167", {"start": v(52.05, 41.65) * mm, "end": v(55.68, 38.03) * mm});
            skLineSegment(sketch, "E201.1.0.168", {"start": v(4.88, 38.03) * mm, "end": v(4.88, 17.97) * mm});
            skPoint(sketch, "E201.1.0.169", {"position": v(80.76, 16.78) * mm});
            skLineSegment(sketch, "E201.1.0.170", {"start": v(87.43, 9) * mm, "end": v(87.43, -17.32) * mm});
            skLineSegment(sketch, "E201.1.0.171", {"start": v(50.22, -18.22) * mm, "end": v(86.53, -18.22) * mm});
            skPoint(sketch, "E201.1.0.172", {"position": v(-1.47, 13.53) * mm});
            skLineSegment(sketch, "E201.1.0.173", {"start": v(-1.47, 44.38) * mm, "end": v(-1.47, 18.04) * mm});
            skPoint(sketch, "E201.1.0.174", {"position": v(81.08, 12.9) * mm});
            skLineSegment(sketch, "E201.1.0.175", {"start": v(84.7, 41.65) * mm, "end": v(81.08, 38.03) * mm});
            skPoint(sketch, "E201.1.0.176", {"position": v(30.28, 13.97) * mm});
            skPoint(sketch, "E201.1.0.177", {"position": v(80.76, 10.28) * mm});
            skPoint(sketch, "E201.1.0.178", {"position": v(30.28, 12.9) * mm});
            skLineSegment(sketch, "E201.1.0.179", {"start": v(2.15, -15.5) * mm, "end": v(5.77, -11.87) * mm});
            skPoint(sketch, "E201.1.0.180", {"position": v(29.96, 10.28) * mm});
            skPoint(sketch, "E201.1.0.181", {"position": v(-1.48, 16.7) * mm});
            skLineSegment(sketch, "E201.1.0.182", {"start": v(2.15, 42.55) * mm, "end": v(5.77, 38.93) * mm});
            skPoint(sketch, "E201.1.0.183", {"position": v(36.63, 13.53) * mm});
            skLineSegment(sketch, "E201.1.0.184", {"start": v(81.08, 38.03) * mm, "end": v(81.08, 17.97) * mm});
            skPoint(sketch, "E201.1.0.185", {"position": v(56, 16.78) * mm});
            skLineSegment(sketch, "E201.1.0.186", {"start": v(49.32, -17.33) * mm, "end": v(49.32, 9.01) * mm});
            skLineSegment(sketch, "E201.1.0.187", {"start": v(1.25, -14.6) * mm, "end": v(4.88, -10.97) * mm});
            skLineSegment(sketch, "E201.1.0.188", {"start": v(35.73, -18.22) * mm, "end": v(-0.58, -18.22) * mm});
            skPoint(sketch, "E201.1.0.189", {"position": v(29.96, 16.78) * mm});
            skPoint(sketch, "E201.1.0.190", {"position": v(87.43, 17.68) * mm});
            skPoint(sketch, "E201.1.0.191", {"position": v(-1.47, -18.22) * mm});
            skPoint(sketch, "E201.1.0.192", {"position": v(36.63, -18.22) * mm});
            skLineSegment(sketch, "E201.1.0.193", {"start": v(87.43, 44.38) * mm, "end": v(87.43, 18.04) * mm});
            skLineSegment(sketch, "E201.1.0.194", {"start": v(33, 42.55) * mm, "end": v(35.73, 45.28) * mm});
            skPoint(sketch, "E201.1.0.195", {"position": v(4.88, 13.53) * mm});
            skPoint(sketch, "E201.1.0.196", {"position": v(30.28, 13.53) * mm});
            skLineSegment(sketch, "E201.1.0.197", {"start": v(1.73, 14.8) * mm, "end": v(-1.4, 17.97) * mm});
            skLineSegment(sketch, "E201.1.0.198", {"start": v(1.73, 12.26) * mm, "end": v(4.88, 9.08) * mm});
            skPoint(sketch, "E201.1.0.199", {"position": v(36.63, 16.77) * mm});
            skLineSegment(sketch, "E201.1.0.200", {"start": v(81.08, 38.03) * mm, "end": v(81.08, 17.97) * mm});
            skLineSegment(sketch, "E201.1.0.201", {"start": v(4.88, 9.08) * mm, "end": v(4.88, -10.97) * mm});
            skLineSegment(sketch, "E201.1.0.202", {"start": v(33.9, 41.65) * mm, "end": v(36.63, 44.38) * mm});
            skLineSegment(sketch, "E201.1.0.203", {"start": v(1.73, 12.26) * mm, "end": v(-1.4, 9.08) * mm});
            skPoint(sketch, "E201.1.0.204", {"position": v(-1.47, 13.53) * mm});
            skPoint(sketch, "E201.1.0.205", {"position": v(49.33, 13.53) * mm});
            skLineSegment(sketch, "E201.1.0.206", {"start": v(4.88, 38.03) * mm, "end": v(4.88, 17.97) * mm});
            skLineSegment(sketch, "E201.1.0.207", {"start": v(-1.47, 44.38) * mm, "end": v(-1.47, 18.04) * mm});
            skLineSegment(sketch, "E201.1.0.208", {"start": v(52.05, 41.65) * mm, "end": v(49.32, 44.38) * mm});
            skLineSegment(sketch, "E201.1.0.209", {"start": v(52.95, 42.55) * mm, "end": v(50.22, 45.28) * mm});
            skPoint(sketch, "E201.1.0.210", {"position": v(36.63, 13.53) * mm});
            skLineSegment(sketch, "E201.1.0.211", {"start": v(84.22, 12.26) * mm, "end": v(81.08, 9.08) * mm});
            skLineSegment(sketch, "E201.1.0.212", {"start": v(52.53, 12.25) * mm, "end": v(55.67, 9.08) * mm});
            skLineSegment(sketch, "E201.1.0.213", {"start": v(1.73, 14.8) * mm, "end": v(4.88, 17.97) * mm});
            skLineSegment(sketch, "E201.1.0.214", {"start": v(-1.47, -17.5) * mm, "end": v(-1.48, 9) * mm});
            skLineSegment(sketch, "E201.1.0.215", {"start": v(81.08, 9.08) * mm, "end": v(81.08, -10.97) * mm});
            skLineSegment(sketch, "E201.1.0.216", {"start": v(87.43, 9) * mm, "end": v(87.43, -17.32) * mm});
            skPoint(sketch, "E201.1.0.217", {"position": v(81.08, 13.53) * mm});
            skPoint(sketch, "E201.1.0.218", {"position": v(87.43, 13.53) * mm});
            skLineSegment(sketch, "E201.1.0.219", {"start": v(84.22, 12.26) * mm, "end": v(87.36, 9.08) * mm});
            skLineSegment(sketch, "E201.1.0.220", {"start": v(52.53, 12.25) * mm, "end": v(49.4, 9.08) * mm});
            skLineSegment(sketch, "E201.1.0.221", {"start": v(84.7, -14.6) * mm, "end": v(87.43, -17.32) * mm});
            skLineSegment(sketch, "E201.1.0.222", {"start": v(33, -15.5) * mm, "end": v(35.73, -18.22) * mm});
            skLineSegment(sketch, "E201.1.0.223", {"start": v(1.25, 41.65) * mm, "end": v(-1.47, 44.38) * mm});
            skPoint(sketch, "E201.1.0.224", {"position": v(36.63, 13.53) * mm});
            skLineSegment(sketch, "E201.1.0.225", {"start": v(84.22, 14.8) * mm, "end": v(81.08, 17.97) * mm});
            skLineSegment(sketch, "E201.1.0.226", {"start": v(33.9, -14.6) * mm, "end": v(36.63, -17.33) * mm});
            skPoint(sketch, "E201.1.0.227", {"position": v(-1.47, 13.53) * mm});
            skLineSegment(sketch, "E201.1.0.228", {"start": v(52.53, 14.8) * mm, "end": v(49.4, 17.97) * mm});
            skLineSegment(sketch, "E201.1.0.229", {"start": v(52.53, 14.8) * mm, "end": v(55.68, 17.97) * mm});
            skLineSegment(sketch, "E201.1.0.230", {"start": v(33.42, 14.8) * mm, "end": v(36.56, 17.97) * mm});
            skLineSegment(sketch, "E201.1.0.231", {"start": v(84.22, 14.8) * mm, "end": v(87.36, 17.97) * mm});
            skLineSegment(sketch, "E201.1.0.232", {"start": v(52.95, -15.5) * mm, "end": v(50.22, -18.22) * mm});
            skPoint(sketch, "E201.1.0.233", {"position": v(49.33, 13.53) * mm});
            skLineSegment(sketch, "E201.1.0.234", {"start": v(33.42, 14.8) * mm, "end": v(30.27, 17.97) * mm});
            skLineSegment(sketch, "E201.1.0.235", {"start": v(33.42, 12.25) * mm, "end": v(30.28, 9.08) * mm});
            skLineSegment(sketch, "E201.1.0.236", {"start": v(83.8, 42.55) * mm, "end": v(86.53, 45.28) * mm});
            skLineSegment(sketch, "E201.1.0.237", {"start": v(52.05, -14.6) * mm, "end": v(49.32, -17.33) * mm});
            skLineSegment(sketch, "E201.1.0.238", {"start": v(87.43, 9) * mm, "end": v(87.43, -17.32) * mm});
            skLineSegment(sketch, "E201.1.0.239", {"start": v(-1.48, 9) * mm, "end": v(-1.47, -17.32) * mm});
            skPoint(sketch, "E201.1.0.240", {"position": v(87.43, 13.53) * mm});
            skLineSegment(sketch, "E201.1.0.241", {"start": v(33.42, 12.25) * mm, "end": v(36.56, 9.08) * mm});
            skLineSegment(sketch, "E201.1.0.242", {"start": v(2.15, 42.55) * mm, "end": v(-0.58, 45.28) * mm});
            skLineSegment(sketch, "E201.1.0.243", {"start": v(83.8, -15.5) * mm, "end": v(86.53, -18.22) * mm});
            skLineSegment(sketch, "E201.1.0.244", {"start": v(2.15, -15.5) * mm, "end": v(-0.58, -18.22) * mm});
            skLineSegment(sketch, "E201.1.0.245", {"start": v(84.7, 41.65) * mm, "end": v(87.43, 44.38) * mm});
            skLineSegment(sketch, "E201.1.0.246", {"start": v(1.25, -14.6) * mm, "end": v(-1.47, -17.32) * mm});
            skLineSegment(sketch, "E201.1.0.247", {"start": v(4.88, 16.7) * mm, "end": v(1.7, 13.53) * mm});
            skLineSegment(sketch, "E201.1.0.248", {"start": v(-1.48, 9) * mm, "end": v(-1.47, -17.32) * mm});
            skLineSegment(sketch, "E201.1.0.249", {"start": v(49.4, 17.97) * mm, "end": v(49.32, 18.04) * mm});
            skLineSegment(sketch, "E201.1.0.250", {"start": v(33.43, 13.54) * mm, "end": v(30.28, 10.35) * mm});
            skLineSegment(sketch, "E201.1.0.251", {"start": v(87.43, -17.32) * mm, "end": v(87.43, 9) * mm});
            skLineSegment(sketch, "E201.1.0.252", {"start": v(52.52, 13.54) * mm, "end": v(55.67, 10.35) * mm});
            skLineSegment(sketch, "E201.1.0.253", {"start": v(30.27, 16.7) * mm, "end": v(33.45, 13.53) * mm});
            skPoint(sketch, "E201.1.0.254", {"position": v(87.43, 13.53) * mm});
            skPoint(sketch, "E201.1.0.255", {"position": v(49.33, 13.53) * mm});
            skPoint(sketch, "E201.1.0.256", {"position": v(-1.47, 13.53) * mm});
            skLineSegment(sketch, "E201.1.0.257", {"start": v(84.23, 13.54) * mm, "end": v(81.08, 10.35) * mm});
            skLineSegment(sketch, "E201.1.0.258", {"start": v(81.08, 16.7) * mm, "end": v(84.25, 13.53) * mm});
            skLineSegment(sketch, "E201.1.0.259", {"start": v(55.68, 16.7) * mm, "end": v(52.5, 13.53) * mm});
            skLineSegment(sketch, "E201.1.0.260", {"start": v(49.4, 9.08) * mm, "end": v(49.32, 9.01) * mm});
            skLineSegment(sketch, "E201.1.0.261", {"start": v(36.56, 17.97) * mm, "end": v(36.63, 18.04) * mm});
            skPoint(sketch, "E201.1.0.262", {"position": v(36.63, 13.53) * mm});
            skLineSegment(sketch, "E201.1.0.263", {"start": v(36.56, 9.08) * mm, "end": v(36.63, 9.01) * mm});
            skPoint(sketch, "E201.1.0.264", {"position": v(49.33, 13.53) * mm});
            skLineSegment(sketch, "E201.1.0.265", {"start": v(-1.4, 17.97) * mm, "end": v(-1.47, 18.04) * mm});
            skPoint(sketch, "E201.1.0.266", {"position": v(-1.47, 13.53) * mm});
            skPoint(sketch, "E201.1.0.267", {"position": v(87.43, 13.53) * mm});
            skLineSegment(sketch, "E201.1.0.268", {"start": v(1.72, 13.54) * mm, "end": v(4.88, 10.35) * mm});
            skPoint(sketch, "E201.1.0.269", {"position": v(36.63, 13.53) * mm});
            skPoint(sketch, "E201.1.0.270", {"position": v(-1.47, 13.53) * mm});
            skPoint(sketch, "E201.1.0.271", {"position": v(36.63, 13.53) * mm});
            skPoint(sketch, "E201.1.0.272", {"position": v(87.43, 13.53) * mm});
            skLineSegment(sketch, "E201.1.0.273", {"start": v(87.36, 17.97) * mm, "end": v(87.43, 18.04) * mm});
            skPoint(sketch, "E201.1.0.274", {"position": v(49.32, 13.53) * mm});
            skPoint(sketch, "E201.1.0.275", {"position": v(-1.47, 13.53) * mm});
            skPoint(sketch, "E201.1.0.276", {"position": v(87.43, 13.53) * mm});
            skPoint(sketch, "E201.1.0.277", {"position": v(36.63, 13.53) * mm});
            skPoint(sketch, "E201.1.0.278", {"position": v(49.32, 13.53) * mm});
            skLineSegment(sketch, "E201.1.0.279", {"start": v(1.7, 13.52) * mm, "end": v(1.7, 13.52) * mm});
            skLineSegment(sketch, "E201.1.0.280", {"start": v(84.25, 13.52) * mm, "end": v(84.25, 13.52) * mm});
            skLineSegment(sketch, "E201.1.0.281", {"start": v(87.36, 9.08) * mm, "end": v(87.43, 9) * mm});
            skLineSegment(sketch, "E201.1.0.282", {"start": v(-1.4, 9.08) * mm, "end": v(-1.48, 9) * mm});
            skLineSegment(sketch, "E201.1.0.283", {"start": v(84.25, 13.52) * mm, "end": v(84.25, 13.53) * mm});
            skLineSegment(sketch, "E201.1.0.284", {"start": v(1.7, 13.53) * mm, "end": v(1.7, 13.52) * mm});
            skLineSegment(sketch, "E201.1.0.285", {"start": v(1.7, 13.52) * mm, "end": v(1.7, 13.53) * mm});
            skLineSegment(sketch, "E201.1.0.286", {"start": v(84.25, 13.53) * mm, "end": v(84.25, 13.52) * mm});
            skLineSegment(sketch, "E201.1.0.287", {"start": v(33.45, 13.56) * mm, "end": v(33.43, 13.54) * mm});
            skLineSegment(sketch, "E201.1.0.288", {"start": v(52.53, 13.53) * mm, "end": v(52.53, 13.56) * mm});
            skLineSegment(sketch, "E201.1.0.289", {"start": v(33.45, 13.56) * mm, "end": v(33.45, 13.53) * mm});
            skLineSegment(sketch, "E201.1.0.290", {"start": v(33.42, 13.53) * mm, "end": v(33.42, 13.56) * mm});
            skLineSegment(sketch, "E201.1.0.291", {"start": v(52.5, 13.56) * mm, "end": v(52.5, 13.53) * mm});
            skLineSegment(sketch, "E201.1.0.292", {"start": v(33.45, 13.53) * mm, "end": v(33.42, 13.53) * mm});
            skLineSegment(sketch, "E201.1.0.293", {"start": v(52.5, 13.53) * mm, "end": v(52.53, 13.53) * mm});
            skLineSegment(sketch, "E201.1.0.294", {"start": v(33.42, 13.53) * mm, "end": v(33.45, 13.53) * mm});
            skLineSegment(sketch, "E201.1.0.295", {"start": v(52.53, 13.53) * mm, "end": v(52.5, 13.53) * mm});
            skLineSegment(sketch, "E201.1.0.296", {"start": v(52.5, 13.56) * mm, "end": v(52.52, 13.54) * mm});
            skPoint(sketch, "E201.2.0.0", {"position": v(106.47, 13.8) * mm});
            skLineSegment(sketch, "E201.2.0.2", {"start": v(144.58, 9.08) * mm, "end": v(144.58, -10.98) * mm});
            skLineSegment(sketch, "E201.2.0.3", {"start": v(144.57, 16.7) * mm, "end": v(119.17, 16.7) * mm});
            skPoint(sketch, "E201.2.0.4", {"position": v(195.38, -11.87) * mm});
            skPoint(sketch, "E201.2.0.6", {"position": v(186.6, -11.87) * mm});
            skPoint(sketch, "E201.2.0.7", {"position": v(166.8, -15.05) * mm});
            skPoint(sketch, "E201.2.0.8", {"position": v(147.75, 10.35) * mm});
            skLineSegment(sketch, "E201.2.0.9", {"start": v(150.03, 45.28) * mm, "end": v(113.72, 45.28) * mm});
            skLineSegment(sketch, "E201.2.0.10", {"start": v(112.83, 44.38) * mm, "end": v(112.83, 18.04) * mm});
            skPoint(sketch, "E201.2.0.11", {"position": v(135.8, -18.22) * mm});
            skPoint(sketch, "E201.2.0.12", {"position": v(150.93, 9.96) * mm});
            skPoint(sketch, "E201.2.0.13", {"position": v(163.62, 9.96) * mm});
            skPoint(sketch, "E201.2.0.14", {"position": v(198.55, -15.05) * mm});
            skLineSegment(sketch, "E201.2.0.15", {"start": v(169.97, 10.35) * mm, "end": v(195.37, 10.35) * mm});
            skPoint(sketch, "E201.2.0.16", {"position": v(195.38, 38.93) * mm});
            skPoint(sketch, "E201.2.0.17", {"position": v(201.73, 45.28) * mm});
            skPoint(sketch, "E201.2.0.19", {"position": v(157.28, -24.57) * mm});
            skLineSegment(sketch, "E201.2.0.20", {"start": v(195.38, 9.08) * mm, "end": v(195.38, -10.97) * mm});
            skPoint(sketch, "E201.2.0.21", {"position": v(147.75, -15.05) * mm});
            skPoint(sketch, "E201.2.0.22", {"position": v(144.26, 16.78) * mm});
            skPoint(sketch, "E201.2.0.23", {"position": v(195.38, 17.1) * mm});
            skPoint(sketch, "E201.2.0.25", {"position": v(163.63, 17.68) * mm});
            skPoint(sketch, "E201.2.0.26", {"position": v(186.6, 38.93) * mm});
            skLineSegment(sketch, "E201.2.0.27", {"start": v(143.68, 38.93) * mm, "end": v(120.07, 38.93) * mm});
            skPoint(sketch, "E201.2.0.28", {"position": v(195.38, 9.96) * mm});
            skLineSegment(sketch, "E201.2.0.29", {"start": v(119.18, 9.08) * mm, "end": v(119.18, -10.97) * mm});
            skPoint(sketch, "E201.2.0.30", {"position": v(169.98, 13.97) * mm});
            skPoint(sketch, "E201.2.0.31", {"position": v(112.83, 17.68) * mm});
            skPoint(sketch, "E201.2.0.32", {"position": v(127.96, 38.93) * mm});
            skLineSegment(sketch, "E201.2.0.34", {"start": v(170.87, 38.93) * mm, "end": v(194.48, 38.93) * mm});
            skLineSegment(sketch, "E201.2.0.35", {"start": v(163.62, 44.38) * mm, "end": v(163.62, 18.04) * mm});
            skLineSegment(sketch, "E201.2.0.36", {"start": v(157.28, 52.19) * mm, "end": v(182.68, 52.19) * mm});
            skLineSegment(sketch, "E201.2.0.37", {"start": v(157.28, -24.01) * mm, "end": v(106.48, -24.01) * mm});
            skPoint(sketch, "E201.2.0.38", {"position": v(150.93, -18.22) * mm});
            skPoint(sketch, "E201.2.0.39", {"position": v(144.58, 12.9) * mm});
            skPoint(sketch, "E201.2.0.40", {"position": v(201.73, 16.77) * mm});
            skPoint(sketch, "E201.2.0.41", {"position": v(144.57, 14.16) * mm});
            skPoint(sketch, "E201.2.0.42", {"position": v(127.96, 45.28) * mm});
            skPoint(sketch, "E201.2.0.43", {"position": v(112.83, 13.53) * mm});
            skPoint(sketch, "E201.2.0.44", {"position": v(178.76, -11.87) * mm});
            skPoint(sketch, "E201.2.0.45", {"position": v(166.8, 42.1) * mm});
            skLineSegment(sketch, "E201.2.0.46", {"start": v(169.97, 9.08) * mm, "end": v(169.97, -10.98) * mm});
            skPoint(sketch, "E201.2.0.47", {"position": v(147.75, 16.7) * mm});
            skPoint(sketch, "E201.2.0.48", {"position": v(112.83, 45.28) * mm});
            skLineSegment(sketch, "E201.2.0.49", {"start": v(208.08, -24.01) * mm, "end": v(157.28, -24.01) * mm});
            skPoint(sketch, "E201.2.0.50", {"position": v(163.62, 45.28) * mm});
            skPoint(sketch, "E201.2.0.51", {"position": v(170.3, 10.28) * mm});
            skLineSegment(sketch, "E201.2.0.52", {"start": v(169.98, 38.03) * mm, "end": v(169.98, 17.97) * mm});
            skLineSegment(sketch, "E201.2.0.53", {"start": v(157.28, 52.19) * mm, "end": v(106.48, 52.19) * mm});
            skPoint(sketch, "E201.2.0.54", {"position": v(208.08, 13.8) * mm});
            skPoint(sketch, "E201.2.0.55", {"position": v(201.73, 13.53) * mm});
            skPoint(sketch, "E201.2.0.56", {"position": v(178.76, 45.28) * mm});
            skPoint(sketch, "E201.2.0.57", {"position": v(119.5, 16.78) * mm});
            skPoint(sketch, "E201.2.0.58", {"position": v(195.06, 10.28) * mm});
            skPoint(sketch, "E201.2.0.59", {"position": v(169.97, 9.96) * mm});
            skPoint(sketch, "E201.2.0.60", {"position": v(186.6, 45.28) * mm});
            skPoint(sketch, "E201.2.0.61", {"position": v(163.62, -18.22) * mm});
            skPoint(sketch, "E201.2.0.62", {"position": v(157.28, 13.8) * mm});
            skPoint(sketch, "E201.2.0.63", {"position": v(169.98, 13.53) * mm});
            skPoint(sketch, "E201.2.0.64", {"position": v(169.98, -11.87) * mm});
            skPoint(sketch, "E201.2.0.65", {"position": v(220.78, 14.09) * mm});
            skPoint(sketch, "E201.2.0.66", {"position": v(208.08, 13.53) * mm});
            skPoint(sketch, "E201.2.0.68", {"position": v(119.18, 12.9) * mm});
            skPoint(sketch, "E201.2.0.69", {"position": v(163.62, 13.53) * mm});
            skPoint(sketch, "E201.2.0.70", {"position": v(214.43, 52.19) * mm});
            skPoint(sketch, "E201.2.0.71", {"position": v(144.58, -11.87) * mm});
            skPoint(sketch, "E201.2.0.72", {"position": v(116, -15.05) * mm});
            skLineSegment(sketch, "E201.2.0.73", {"start": v(201.73, 44.38) * mm, "end": v(201.73, 18.04) * mm});
            skPoint(sketch, "E201.2.0.74", {"position": v(182.68, -24.57) * mm});
            skPoint(sketch, "E201.2.0.75", {"position": v(169.98, 12.9) * mm});
            skPoint(sketch, "E201.2.0.76", {"position": v(163.62, 17.1) * mm});
            skPoint(sketch, "E201.2.0.77", {"position": v(119.18, -11.87) * mm});
            skLineSegment(sketch, "E201.2.0.78", {"start": v(163.62, 9.01) * mm, "end": v(163.62, -17.33) * mm});
            skPoint(sketch, "E201.2.0.79", {"position": v(178.76, 38.93) * mm});
            skLineSegment(sketch, "E201.2.0.80", {"start": v(170.87, -11.87) * mm, "end": v(194.48, -11.87) * mm});
            skLineSegment(sketch, "E201.2.0.81", {"start": v(119.18, 38.03) * mm, "end": v(119.18, 17.97) * mm});
            skPoint(sketch, "E201.2.0.82", {"position": v(116, 42.1) * mm});
            skPoint(sketch, "E201.2.0.83", {"position": v(166.8, 10.35) * mm});
            skPoint(sketch, "E201.2.0.84", {"position": v(163.63, 16.7) * mm});
            skPoint(sketch, "E201.2.0.85", {"position": v(150.93, 17.68) * mm});
            skPoint(sketch, "E201.2.0.86", {"position": v(178.76, -18.22) * mm});
            skPoint(sketch, "E201.2.0.87", {"position": v(195.38, 12.9) * mm});
            skPoint(sketch, "E201.2.0.88", {"position": v(169.98, 38.93) * mm});
            skPoint(sketch, "E201.2.0.89", {"position": v(119.5, 10.28) * mm});
            skPoint(sketch, "E201.2.0.90", {"position": v(150.93, 13.53) * mm});
            skPoint(sketch, "E201.2.0.91", {"position": v(208.08, -24.57) * mm});
            skLineSegment(sketch, "E201.2.0.92", {"start": v(164.52, 45.28) * mm, "end": v(200.83, 45.28) * mm});
            skLineSegment(sketch, "E201.2.0.93", {"start": v(164.52, -18.22) * mm, "end": v(200.83, -18.22) * mm});
            skPoint(sketch, "E201.2.0.94", {"position": v(144.58, 9.96) * mm});
            skPoint(sketch, "E201.2.0.95", {"position": v(144.26, 10.28) * mm});
            skLineSegment(sketch, "E201.2.0.96", {"start": v(144.57, 38.03) * mm, "end": v(144.57, 17.97) * mm});
            skLineSegment(sketch, "E201.2.0.97", {"start": v(144.58, 10.35) * mm, "end": v(119.18, 10.35) * mm});
            skPoint(sketch, "E201.2.0.98", {"position": v(201.73, -18.22) * mm});
            skPoint(sketch, "E201.2.0.99", {"position": v(166.8, 16.7) * mm});
            skPoint(sketch, "E201.2.0.100", {"position": v(144.57, 38.93) * mm});
            skLineSegment(sketch, "E201.2.0.101", {"start": v(112.83, -17.32) * mm, "end": v(112.82, 9) * mm});
            skPoint(sketch, "E201.2.0.102", {"position": v(150.93, 45.28) * mm});
            skPoint(sketch, "E201.2.0.103", {"position": v(119.18, 17.1) * mm});
            skPoint(sketch, "E201.2.0.104", {"position": v(119.18, 9.96) * mm});
            skLineSegment(sketch, "E201.2.0.105", {"start": v(182.68, 52.19) * mm, "end": v(208.08, 52.19) * mm});
            skLineSegment(sketch, "E201.2.0.106", {"start": v(143.68, -11.87) * mm, "end": v(120.07, -11.87) * mm});
            skPoint(sketch, "E201.2.0.107", {"position": v(127.96, -11.87) * mm});
            skPoint(sketch, "E201.2.0.108", {"position": v(208.08, 51.63) * mm});
            skPoint(sketch, "E201.2.0.109", {"position": v(106.48, 13.53) * mm});
            skLineSegment(sketch, "E201.2.0.110", {"start": v(150.03, -18.22) * mm, "end": v(113.72, -18.22) * mm});
            skPoint(sketch, "E201.2.0.111", {"position": v(119.18, 38.93) * mm});
            skPoint(sketch, "E201.2.0.112", {"position": v(135.8, -11.87) * mm});
            skLineSegment(sketch, "E201.2.0.113", {"start": v(150.93, 44.38) * mm, "end": v(150.93, 18.04) * mm});
            skPoint(sketch, "E201.2.0.115", {"position": v(135.8, 45.28) * mm});
            skLineSegment(sketch, "E201.2.0.116", {"start": v(150.93, -17.33) * mm, "end": v(150.93, 9.01) * mm});
            skPoint(sketch, "E201.2.0.117", {"position": v(135.8, 38.93) * mm});
            skLineSegment(sketch, "E201.2.0.118", {"start": v(169.98, 16.7) * mm, "end": v(195.38, 16.7) * mm});
            skPoint(sketch, "E201.2.0.119", {"position": v(127.96, -18.22) * mm});
            skPoint(sketch, "E201.2.0.120", {"position": v(147.75, 42.1) * mm});
            skPoint(sketch, "E201.2.0.121", {"position": v(198.55, 42.1) * mm});
            skPoint(sketch, "E201.2.0.122", {"position": v(186.6, -18.22) * mm});
            skPoint(sketch, "E201.2.0.123", {"position": v(170.3, 16.78) * mm});
            skPoint(sketch, "E201.2.0.124", {"position": v(214.43, -24.01) * mm});
            skPoint(sketch, "E201.2.0.125", {"position": v(195.06, 16.78) * mm});
            skPoint(sketch, "E201.2.0.126", {"position": v(112.83, -18.22) * mm});
            skLineSegment(sketch, "E201.2.0.127", {"start": v(195.38, 38.03) * mm, "end": v(195.38, 17.97) * mm});
            skPoint(sketch, "E201.2.0.128", {"position": v(112.82, 16.77) * mm});
            skLineSegment(sketch, "E201.2.0.129", {"start": v(201.73, -17.5) * mm, "end": v(201.73, 9) * mm});
            skPoint(sketch, "E201.2.0.130", {"position": v(150.92, 16.7) * mm});
            skLineSegment(sketch, "E201.2.0.131", {"start": v(170.87, -11.87) * mm, "end": v(194.48, -11.87) * mm});
            skLineSegment(sketch, "E201.2.0.132", {"start": v(119.18, 9.08) * mm, "end": v(119.18, -10.97) * mm});
            skPoint(sketch, "E201.2.0.133", {"position": v(169.98, 14.16) * mm});
            skPoint(sketch, "E201.2.0.134", {"position": v(163.63, -18.22) * mm});
            skPoint(sketch, "E201.2.0.135", {"position": v(119.18, 12.9) * mm});
            skPoint(sketch, "E201.2.0.136", {"position": v(150.93, 17.1) * mm});
            skLineSegment(sketch, "E201.2.0.137", {"start": v(195.38, 9.08) * mm, "end": v(195.38, -10.97) * mm});
            skLineSegment(sketch, "E201.2.0.138", {"start": v(150.93, 9.01) * mm, "end": v(150.93, -17.33) * mm});
            skLineSegment(sketch, "E201.2.0.139", {"start": v(147.3, 42.55) * mm, "end": v(143.68, 38.93) * mm});
            skPoint(sketch, "E201.2.0.140", {"position": v(112.83, 45.28) * mm});
            skLineSegment(sketch, "E201.2.0.141", {"start": v(166.35, -14.6) * mm, "end": v(169.97, -10.98) * mm});
            skLineSegment(sketch, "E201.2.0.142", {"start": v(115.55, 41.65) * mm, "end": v(119.18, 38.03) * mm});
            skLineSegment(sketch, "E201.2.0.143", {"start": v(199, -14.6) * mm, "end": v(195.38, -10.97) * mm});
            skLineSegment(sketch, "E201.2.0.144", {"start": v(167.25, -15.5) * mm, "end": v(170.87, -11.87) * mm});
            skPoint(sketch, "E201.2.0.145", {"position": v(119.5, 10.28) * mm});
            skPoint(sketch, "E201.2.0.146", {"position": v(195.38, 14.16) * mm});
            skPoint(sketch, "E201.2.0.147", {"position": v(170.3, 10.28) * mm});
            skPoint(sketch, "E201.2.0.148", {"position": v(163.63, 16.77) * mm});
            skPoint(sketch, "E201.2.0.149", {"position": v(201.73, 45.28) * mm});
            skPoint(sketch, "E201.2.0.150", {"position": v(201.73, 13.53) * mm});
            skPoint(sketch, "E201.2.0.151", {"position": v(169.98, 12.9) * mm});
            skPoint(sketch, "E201.2.0.152", {"position": v(208.08, -24.57) * mm});
            skPoint(sketch, "E201.2.0.153", {"position": v(119.18, 14.16) * mm});
            skLineSegment(sketch, "E201.2.0.154", {"start": v(148.2, -14.6) * mm, "end": v(144.58, -10.98) * mm});
            skLineSegment(sketch, "E201.2.0.155", {"start": v(143.68, -11.87) * mm, "end": v(120.07, -11.87) * mm});
            skPoint(sketch, "E201.2.0.156", {"position": v(201.73, -18.22) * mm});
            skPoint(sketch, "E201.2.0.157", {"position": v(119.5, 16.78) * mm});
            skPoint(sketch, "E201.2.0.158", {"position": v(201.73, 16.7) * mm});
            skLineSegment(sketch, "E201.2.0.159", {"start": v(147.3, -15.5) * mm, "end": v(143.68, -11.87) * mm});
            skLineSegment(sketch, "E201.2.0.160", {"start": v(198.1, -15.5) * mm, "end": v(194.48, -11.87) * mm});
            skLineSegment(sketch, "E201.2.0.161", {"start": v(112.82, 9) * mm, "end": v(112.83, -17.32) * mm});
            skLineSegment(sketch, "E201.2.0.162", {"start": v(167.25, 42.55) * mm, "end": v(170.87, 38.93) * mm});
            skLineSegment(sketch, "E201.2.0.163", {"start": v(201.73, 44.38) * mm, "end": v(201.73, 18.04) * mm});
            skLineSegment(sketch, "E201.2.0.164", {"start": v(148.2, 41.65) * mm, "end": v(144.57, 38.03) * mm});
            skPoint(sketch, "E201.2.0.165", {"position": v(163.63, 13.53) * mm});
            skLineSegment(sketch, "E201.2.0.166", {"start": v(198.1, 42.55) * mm, "end": v(194.48, 38.93) * mm});
            skLineSegment(sketch, "E201.2.0.167", {"start": v(166.35, 41.65) * mm, "end": v(169.98, 38.03) * mm});
            skLineSegment(sketch, "E201.2.0.168", {"start": v(119.18, 38.03) * mm, "end": v(119.18, 17.97) * mm});
            skPoint(sketch, "E201.2.0.169", {"position": v(195.06, 16.78) * mm});
            skLineSegment(sketch, "E201.2.0.170", {"start": v(201.73, 9) * mm, "end": v(201.73, -17.32) * mm});
            skLineSegment(sketch, "E201.2.0.171", {"start": v(164.52, -18.22) * mm, "end": v(200.83, -18.22) * mm});
            skPoint(sketch, "E201.2.0.172", {"position": v(112.83, 13.53) * mm});
            skLineSegment(sketch, "E201.2.0.173", {"start": v(112.83, 44.38) * mm, "end": v(112.83, 18.04) * mm});
            skPoint(sketch, "E201.2.0.174", {"position": v(195.38, 12.9) * mm});
            skLineSegment(sketch, "E201.2.0.175", {"start": v(199, 41.65) * mm, "end": v(195.38, 38.03) * mm});
            skPoint(sketch, "E201.2.0.176", {"position": v(144.58, 13.97) * mm});
            skPoint(sketch, "E201.2.0.177", {"position": v(195.06, 10.28) * mm});
            skPoint(sketch, "E201.2.0.178", {"position": v(144.58, 12.9) * mm});
            skLineSegment(sketch, "E201.2.0.179", {"start": v(116.45, -15.5) * mm, "end": v(120.07, -11.87) * mm});
            skPoint(sketch, "E201.2.0.180", {"position": v(144.26, 10.28) * mm});
            skPoint(sketch, "E201.2.0.181", {"position": v(112.82, 16.7) * mm});
            skLineSegment(sketch, "E201.2.0.182", {"start": v(116.45, 42.55) * mm, "end": v(120.07, 38.93) * mm});
            skPoint(sketch, "E201.2.0.183", {"position": v(150.93, 13.53) * mm});
            skLineSegment(sketch, "E201.2.0.184", {"start": v(195.38, 38.03) * mm, "end": v(195.38, 17.97) * mm});
            skPoint(sketch, "E201.2.0.185", {"position": v(170.3, 16.78) * mm});
            skLineSegment(sketch, "E201.2.0.186", {"start": v(163.62, -17.33) * mm, "end": v(163.62, 9.01) * mm});
            skLineSegment(sketch, "E201.2.0.187", {"start": v(115.55, -14.6) * mm, "end": v(119.18, -10.97) * mm});
            skLineSegment(sketch, "E201.2.0.188", {"start": v(150.03, -18.22) * mm, "end": v(113.72, -18.22) * mm});
            skPoint(sketch, "E201.2.0.189", {"position": v(144.26, 16.78) * mm});
            skPoint(sketch, "E201.2.0.190", {"position": v(201.73, 17.68) * mm});
            skPoint(sketch, "E201.2.0.191", {"position": v(112.83, -18.22) * mm});
            skPoint(sketch, "E201.2.0.192", {"position": v(150.93, -18.22) * mm});
            skLineSegment(sketch, "E201.2.0.193", {"start": v(201.73, 44.38) * mm, "end": v(201.73, 18.04) * mm});
            skLineSegment(sketch, "E201.2.0.194", {"start": v(147.3, 42.55) * mm, "end": v(150.03, 45.28) * mm});
            skPoint(sketch, "E201.2.0.195", {"position": v(119.18, 13.53) * mm});
            skPoint(sketch, "E201.2.0.196", {"position": v(144.58, 13.53) * mm});
            skLineSegment(sketch, "E201.2.0.197", {"start": v(116.03, 14.8) * mm, "end": v(112.9, 17.97) * mm});
            skLineSegment(sketch, "E201.2.0.198", {"start": v(116.03, 12.26) * mm, "end": v(119.18, 9.08) * mm});
            skPoint(sketch, "E201.2.0.199", {"position": v(150.93, 16.77) * mm});
            skLineSegment(sketch, "E201.2.0.200", {"start": v(195.38, 38.03) * mm, "end": v(195.38, 17.97) * mm});
            skLineSegment(sketch, "E201.2.0.201", {"start": v(119.18, 9.08) * mm, "end": v(119.18, -10.97) * mm});
            skLineSegment(sketch, "E201.2.0.202", {"start": v(148.2, 41.65) * mm, "end": v(150.93, 44.38) * mm});
            skLineSegment(sketch, "E201.2.0.203", {"start": v(116.03, 12.26) * mm, "end": v(112.9, 9.08) * mm});
            skPoint(sketch, "E201.2.0.204", {"position": v(112.83, 13.53) * mm});
            skPoint(sketch, "E201.2.0.205", {"position": v(163.63, 13.53) * mm});
            skLineSegment(sketch, "E201.2.0.206", {"start": v(119.18, 38.03) * mm, "end": v(119.18, 17.97) * mm});
            skLineSegment(sketch, "E201.2.0.207", {"start": v(112.83, 44.38) * mm, "end": v(112.83, 18.04) * mm});
            skLineSegment(sketch, "E201.2.0.208", {"start": v(166.35, 41.65) * mm, "end": v(163.62, 44.38) * mm});
            skLineSegment(sketch, "E201.2.0.209", {"start": v(167.25, 42.55) * mm, "end": v(164.52, 45.28) * mm});
            skPoint(sketch, "E201.2.0.210", {"position": v(150.93, 13.53) * mm});
            skLineSegment(sketch, "E201.2.0.211", {"start": v(198.52, 12.26) * mm, "end": v(195.38, 9.08) * mm});
            skLineSegment(sketch, "E201.2.0.212", {"start": v(166.83, 12.25) * mm, "end": v(169.97, 9.08) * mm});
            skLineSegment(sketch, "E201.2.0.213", {"start": v(116.03, 14.8) * mm, "end": v(119.18, 17.97) * mm});
            skLineSegment(sketch, "E201.2.0.214", {"start": v(112.83, -17.5) * mm, "end": v(112.82, 9) * mm});
            skLineSegment(sketch, "E201.2.0.215", {"start": v(195.38, 9.08) * mm, "end": v(195.38, -10.97) * mm});
            skLineSegment(sketch, "E201.2.0.216", {"start": v(201.73, 9) * mm, "end": v(201.73, -17.32) * mm});
            skPoint(sketch, "E201.2.0.217", {"position": v(195.38, 13.53) * mm});
            skPoint(sketch, "E201.2.0.218", {"position": v(201.73, 13.53) * mm});
            skLineSegment(sketch, "E201.2.0.219", {"start": v(198.52, 12.26) * mm, "end": v(201.66, 9.08) * mm});
            skLineSegment(sketch, "E201.2.0.220", {"start": v(166.83, 12.25) * mm, "end": v(163.7, 9.08) * mm});
            skLineSegment(sketch, "E201.2.0.221", {"start": v(199, -14.6) * mm, "end": v(201.73, -17.32) * mm});
            skLineSegment(sketch, "E201.2.0.222", {"start": v(147.3, -15.5) * mm, "end": v(150.03, -18.22) * mm});
            skLineSegment(sketch, "E201.2.0.223", {"start": v(115.55, 41.65) * mm, "end": v(112.83, 44.38) * mm});
            skPoint(sketch, "E201.2.0.224", {"position": v(150.93, 13.53) * mm});
            skLineSegment(sketch, "E201.2.0.225", {"start": v(198.52, 14.8) * mm, "end": v(195.38, 17.97) * mm});
            skLineSegment(sketch, "E201.2.0.226", {"start": v(148.2, -14.6) * mm, "end": v(150.93, -17.33) * mm});
            skPoint(sketch, "E201.2.0.227", {"position": v(112.83, 13.53) * mm});
            skLineSegment(sketch, "E201.2.0.228", {"start": v(166.83, 14.8) * mm, "end": v(163.7, 17.97) * mm});
            skLineSegment(sketch, "E201.2.0.229", {"start": v(166.83, 14.8) * mm, "end": v(169.98, 17.97) * mm});
            skLineSegment(sketch, "E201.2.0.230", {"start": v(147.72, 14.8) * mm, "end": v(150.86, 17.97) * mm});
            skLineSegment(sketch, "E201.2.0.231", {"start": v(198.52, 14.8) * mm, "end": v(201.66, 17.97) * mm});
            skLineSegment(sketch, "E201.2.0.232", {"start": v(167.25, -15.5) * mm, "end": v(164.52, -18.22) * mm});
            skPoint(sketch, "E201.2.0.233", {"position": v(163.63, 13.53) * mm});
            skLineSegment(sketch, "E201.2.0.234", {"start": v(147.72, 14.8) * mm, "end": v(144.57, 17.97) * mm});
            skLineSegment(sketch, "E201.2.0.235", {"start": v(147.72, 12.25) * mm, "end": v(144.58, 9.08) * mm});
            skLineSegment(sketch, "E201.2.0.236", {"start": v(198.1, 42.55) * mm, "end": v(200.83, 45.28) * mm});
            skLineSegment(sketch, "E201.2.0.237", {"start": v(166.35, -14.6) * mm, "end": v(163.62, -17.33) * mm});
            skLineSegment(sketch, "E201.2.0.238", {"start": v(201.73, 9) * mm, "end": v(201.73, -17.32) * mm});
            skLineSegment(sketch, "E201.2.0.239", {"start": v(112.82, 9) * mm, "end": v(112.83, -17.32) * mm});
            skPoint(sketch, "E201.2.0.240", {"position": v(201.73, 13.53) * mm});
            skLineSegment(sketch, "E201.2.0.241", {"start": v(147.72, 12.25) * mm, "end": v(150.86, 9.08) * mm});
            skLineSegment(sketch, "E201.2.0.242", {"start": v(116.45, 42.55) * mm, "end": v(113.72, 45.28) * mm});
            skLineSegment(sketch, "E201.2.0.243", {"start": v(198.1, -15.5) * mm, "end": v(200.83, -18.22) * mm});
            skLineSegment(sketch, "E201.2.0.244", {"start": v(116.45, -15.5) * mm, "end": v(113.72, -18.22) * mm});
            skLineSegment(sketch, "E201.2.0.245", {"start": v(199, 41.65) * mm, "end": v(201.73, 44.38) * mm});
            skLineSegment(sketch, "E201.2.0.246", {"start": v(115.55, -14.6) * mm, "end": v(112.83, -17.32) * mm});
            skLineSegment(sketch, "E201.2.0.247", {"start": v(119.18, 16.7) * mm, "end": v(116, 13.53) * mm});
            skLineSegment(sketch, "E201.2.0.248", {"start": v(112.82, 9) * mm, "end": v(112.83, -17.32) * mm});
            skLineSegment(sketch, "E201.2.0.249", {"start": v(163.7, 17.97) * mm, "end": v(163.62, 18.04) * mm});
            skLineSegment(sketch, "E201.2.0.250", {"start": v(147.73, 13.54) * mm, "end": v(144.58, 10.35) * mm});
            skLineSegment(sketch, "E201.2.0.251", {"start": v(201.73, -17.32) * mm, "end": v(201.73, 9) * mm});
            skLineSegment(sketch, "E201.2.0.252", {"start": v(166.82, 13.54) * mm, "end": v(169.97, 10.35) * mm});
            skLineSegment(sketch, "E201.2.0.253", {"start": v(144.57, 16.7) * mm, "end": v(147.75, 13.53) * mm});
            skPoint(sketch, "E201.2.0.254", {"position": v(201.73, 13.53) * mm});
            skPoint(sketch, "E201.2.0.255", {"position": v(163.63, 13.53) * mm});
            skPoint(sketch, "E201.2.0.256", {"position": v(112.83, 13.53) * mm});
            skLineSegment(sketch, "E201.2.0.257", {"start": v(198.53, 13.54) * mm, "end": v(195.38, 10.35) * mm});
            skLineSegment(sketch, "E201.2.0.258", {"start": v(195.38, 16.7) * mm, "end": v(198.55, 13.53) * mm});
            skLineSegment(sketch, "E201.2.0.259", {"start": v(169.98, 16.7) * mm, "end": v(166.8, 13.53) * mm});
            skLineSegment(sketch, "E201.2.0.260", {"start": v(163.7, 9.08) * mm, "end": v(163.62, 9.01) * mm});
            skLineSegment(sketch, "E201.2.0.261", {"start": v(150.86, 17.97) * mm, "end": v(150.93, 18.04) * mm});
            skPoint(sketch, "E201.2.0.262", {"position": v(150.93, 13.53) * mm});
            skLineSegment(sketch, "E201.2.0.263", {"start": v(150.86, 9.08) * mm, "end": v(150.93, 9.01) * mm});
            skPoint(sketch, "E201.2.0.264", {"position": v(163.63, 13.53) * mm});
            skLineSegment(sketch, "E201.2.0.265", {"start": v(112.9, 17.97) * mm, "end": v(112.83, 18.04) * mm});
            skPoint(sketch, "E201.2.0.266", {"position": v(112.83, 13.53) * mm});
            skPoint(sketch, "E201.2.0.267", {"position": v(201.73, 13.53) * mm});
            skLineSegment(sketch, "E201.2.0.268", {"start": v(116.02, 13.54) * mm, "end": v(119.18, 10.35) * mm});
            skPoint(sketch, "E201.2.0.269", {"position": v(150.93, 13.53) * mm});
            skPoint(sketch, "E201.2.0.270", {"position": v(112.83, 13.53) * mm});
            skPoint(sketch, "E201.2.0.271", {"position": v(150.93, 13.53) * mm});
            skPoint(sketch, "E201.2.0.272", {"position": v(201.73, 13.53) * mm});
            skLineSegment(sketch, "E201.2.0.273", {"start": v(201.66, 17.97) * mm, "end": v(201.73, 18.04) * mm});
            skPoint(sketch, "E201.2.0.274", {"position": v(163.62, 13.53) * mm});
            skPoint(sketch, "E201.2.0.275", {"position": v(112.83, 13.53) * mm});
            skPoint(sketch, "E201.2.0.276", {"position": v(201.73, 13.53) * mm});
            skPoint(sketch, "E201.2.0.277", {"position": v(150.93, 13.53) * mm});
            skPoint(sketch, "E201.2.0.278", {"position": v(163.62, 13.53) * mm});
            skLineSegment(sketch, "E201.2.0.279", {"start": v(116, 13.52) * mm, "end": v(116, 13.52) * mm});
            skLineSegment(sketch, "E201.2.0.280", {"start": v(198.55, 13.52) * mm, "end": v(198.55, 13.52) * mm});
            skLineSegment(sketch, "E201.2.0.281", {"start": v(201.66, 9.08) * mm, "end": v(201.73, 9) * mm});
            skLineSegment(sketch, "E201.2.0.282", {"start": v(112.9, 9.08) * mm, "end": v(112.82, 9) * mm});
            skLineSegment(sketch, "E201.2.0.283", {"start": v(198.55, 13.52) * mm, "end": v(198.55, 13.53) * mm});
            skLineSegment(sketch, "E201.2.0.284", {"start": v(116, 13.53) * mm, "end": v(116, 13.52) * mm});
            skLineSegment(sketch, "E201.2.0.285", {"start": v(116, 13.52) * mm, "end": v(116, 13.53) * mm});
            skLineSegment(sketch, "E201.2.0.286", {"start": v(198.55, 13.53) * mm, "end": v(198.55, 13.52) * mm});
            skLineSegment(sketch, "E201.2.0.287", {"start": v(147.75, 13.56) * mm, "end": v(147.73, 13.54) * mm});
            skLineSegment(sketch, "E201.2.0.288", {"start": v(166.83, 13.53) * mm, "end": v(166.83, 13.56) * mm});
            skLineSegment(sketch, "E201.2.0.289", {"start": v(147.75, 13.56) * mm, "end": v(147.75, 13.53) * mm});
            skLineSegment(sketch, "E201.2.0.290", {"start": v(147.72, 13.53) * mm, "end": v(147.72, 13.56) * mm});
            skLineSegment(sketch, "E201.2.0.291", {"start": v(166.8, 13.56) * mm, "end": v(166.8, 13.53) * mm});
            skLineSegment(sketch, "E201.2.0.292", {"start": v(147.75, 13.53) * mm, "end": v(147.72, 13.53) * mm});
            skLineSegment(sketch, "E201.2.0.293", {"start": v(166.8, 13.53) * mm, "end": v(166.83, 13.53) * mm});
            skLineSegment(sketch, "E201.2.0.294", {"start": v(147.72, 13.53) * mm, "end": v(147.75, 13.53) * mm});
            skLineSegment(sketch, "E201.2.0.295", {"start": v(166.83, 13.53) * mm, "end": v(166.8, 13.53) * mm});
            skLineSegment(sketch, "E201.2.0.296", {"start": v(166.8, 13.56) * mm, "end": v(166.82, 13.54) * mm});
            skLineSegment(sketch, "E201.direction1", {"start": v(-122.12, -24.01) * mm, "end": v(-7.82, -24.01) * mm, "construction": true});
            skLineSegment(sketch, "E202", {"start": v(208.08, 52.19) * mm, "end": v(208.08, -24.01) * mm});
            skPoint(sketch, "E203.orphan", {"position": v(220.78, -24.01) * mm});
            skLineSegment(sketch, "E204", {"start": v(-61.78, 13.54) * mm, "end": v(-61.78, 13.54) * mm});
            skPoint(sketch, "E205.trimOffspring.end.orphan", {"position": v(-61.8, 13.53) * mm});
            skPoint(sketch, "E206", {"position": v(-109.43, 16.7) * mm});
            skLineSegment(sketch, "E207", {"start": v(-109.43, 10.35) * mm, "end": v(-109.42, 10.35) * mm});
            skLineSegment(sketch, "E208", {"start": v(-33.23, 10.35) * mm, "end": v(-33.22, 10.35) * mm});
            skLineSegment(sketch, "E209", {"start": v(4.88, 10.35) * mm, "end": v(4.88, 10.35) * mm});
            skLineSegment(sketch, "E210", {"start": v(81.07, 10.35) * mm, "end": v(81.08, 10.35) * mm});
            skLineSegment(sketch, "E211", {"start": v(119.18, 10.35) * mm, "end": v(119.18, 10.35) * mm});
            skLineSegment(sketch, "E212", {"start": v(195.37, 10.35) * mm, "end": v(195.38, 10.35) * mm});
            skSolve(sketch);
        }
        {
            var Q0;
            Q0=makeQuery(id+"F0.imprint","IMPRINT",FACE,{"disambiguationData":[TD([[makeQuery(id+"F0.imprint","IMPRINT",EDGE,{"derivedFrom":sQuery(id+"F0.wireOp",EDGE,"E0.bottom")}),-1.0]])]});
            extrude(context, id + "F1", {"entities" : qUnion([Q0]), "depth" : 25.4 * mm});
        }
    });
